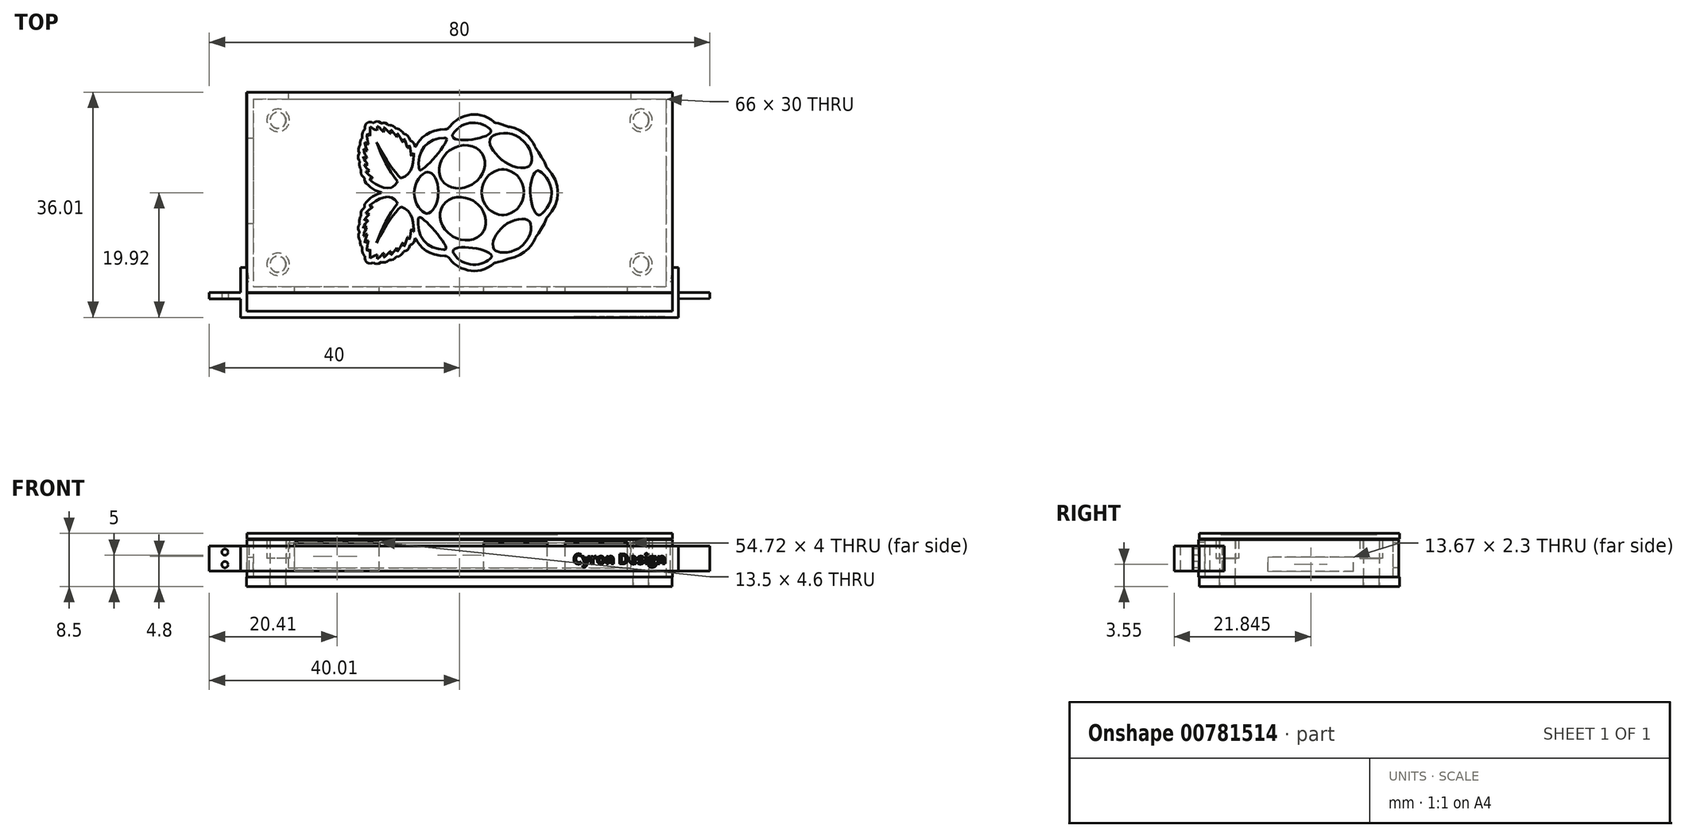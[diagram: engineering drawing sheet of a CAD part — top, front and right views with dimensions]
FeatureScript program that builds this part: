
annotation { "Feature Type Name" : "Feature", "Feature Type Description" : "" }
export const myFeature = defineFeature(function(context is Context, id is Id, definition is map)
    precondition{}
    {
        {
            var Q0;
            Q0=qCreatedBy(makeId("Top.planeOp"),FACE);
            var sketch = newSketch(context, id + "F0", { "sketchPlane" : qUnion([Q0])});
            skLineSegment(sketch, "E0.bottom", {"start": v(-34, 15.91) * mm, "end": v(34, 15.91) * mm});
            skLineSegment(sketch, "E0.top", {"start": v(-34, -16.09) * mm, "end": v(34, -16.09) * mm});
            skLineSegment(sketch, "E0.left", {"start": v(-34, 15.91) * mm, "end": v(-34, -16.09) * mm});
            skLineSegment(sketch, "E0.right", {"start": v(34, 15.91) * mm, "end": v(34, -16.09) * mm});
            skLineSegment(sketch, "E1.bottom", {"start": v(-33, 14.91) * mm, "end": v(33, 14.91) * mm});
            skLineSegment(sketch, "E1.top", {"start": v(-33, -15.09) * mm, "end": v(33, -15.09) * mm});
            skLineSegment(sketch, "E1.left", {"start": v(-33, 14.91) * mm, "end": v(-33, -15.09) * mm});
            skLineSegment(sketch, "E1.right", {"start": v(33, 14.91) * mm, "end": v(33, -15.09) * mm});
            skPoint(sketch, "E2", {"position": v(0, -15.09) * mm});
            skPoint(sketch, "E3", {"position": v(0, -16.09) * mm});
            skPoint(sketch, "E4", {"position": v(0, 14.91) * mm});
            skPoint(sketch, "E5", {"position": v(0, 15.91) * mm});
            skPoint(sketch, "E6", {"position": v(-34, -0.09) * mm});
            skPoint(sketch, "E7", {"position": v(-33, -0.09) * mm});
            skPoint(sketch, "E8", {"position": v(33, -0.09) * mm});
            skPoint(sketch, "E9", {"position": v(34, -0.09) * mm});
            skSolve(sketch);
        }
        {
            var Q0;
            Q0=qCreatedBy(makeId("Top.planeOp"),FACE);
            var sketch = newSketch(context, id + "F1", { "sketchPlane" : qUnion([Q0])});
            skLineSegment(sketch, "E10.bottom", {"start": v(-26.34, -17.54) * mm, "end": v(-12.84, -17.54) * mm});
            skLineSegment(sketch, "E10.top", {"start": v(-26.34, -9.55) * mm, "end": v(-12.84, -9.55) * mm});
            skLineSegment(sketch, "E10.left", {"start": v(-26.34, -17.54) * mm, "end": v(-26.34, -9.55) * mm});
            skLineSegment(sketch, "E10.right", {"start": v(-12.84, -17.54) * mm, "end": v(-12.84, -9.55) * mm});
            skLineSegment(sketch, "E11.bottom", {"start": v(3.84, -17.54) * mm, "end": v(14.02, -17.54) * mm});
            skLineSegment(sketch, "E11.top", {"start": v(3.84, -9.55) * mm, "end": v(14.02, -9.55) * mm});
            skLineSegment(sketch, "E11.left", {"start": v(3.84, -17.54) * mm, "end": v(3.84, -9.55) * mm});
            skLineSegment(sketch, "E11.right", {"start": v(14.02, -17.54) * mm, "end": v(14.02, -9.55) * mm});
            skLineSegment(sketch, "E12.bottom", {"start": v(16.87, -17.41) * mm, "end": v(26.88, -17.41) * mm});
            skLineSegment(sketch, "E12.top", {"start": v(16.87, -9.55) * mm, "end": v(26.88, -9.55) * mm});
            skLineSegment(sketch, "E12.left", {"start": v(16.87, -17.41) * mm, "end": v(16.87, -9.55) * mm});
            skLineSegment(sketch, "E12.right", {"start": v(26.88, -17.41) * mm, "end": v(26.88, -9.55) * mm});
            skSolve(sketch);
        }
        {
            var Q0;
            Q0=qSketchRegion(id+"F0",true);
            extrude(context, id + "F2", {"entities" : qUnion([Q0]), "depth" : 6 * mm, "offsetDistance" : 25 * mm});
        }
        {
            var Q0;
            Q0=qCreatedBy(makeId("Top.planeOp"),FACE);
            var sketch = newSketch(context, id + "F3", { "sketchPlane" : qUnion([Q0])});
            skLineSegment(sketch, "E13.bottom", {"start": v(-35.27, 8.67) * mm, "end": v(-25.56, 8.67) * mm});
            skLineSegment(sketch, "E13.top", {"start": v(-35.27, -5) * mm, "end": v(-25.56, -5) * mm});
            skLineSegment(sketch, "E13.left", {"start": v(-35.27, 8.67) * mm, "end": v(-35.27, -5) * mm});
            skLineSegment(sketch, "E13.right", {"start": v(-25.56, 8.67) * mm, "end": v(-25.56, -5) * mm});
            skSolve(sketch);
        }
        {
            var Q0;
            Q0=qCreatedBy(makeId("Top.planeOp"),FACE);
            var sketch = newSketch(context, id + "F4", { "sketchPlane" : qUnion([Q0])});
            skLineSegment(sketch, "E14.bottom", {"start": v(-27.35, 17.47) * mm, "end": v(27.37, 17.47) * mm});
            skLineSegment(sketch, "E14.top", {"start": v(-27.35, 9.27) * mm, "end": v(27.37, 9.27) * mm});
            skLineSegment(sketch, "E14.left", {"start": v(-27.35, 17.47) * mm, "end": v(-27.35, 9.27) * mm});
            skLineSegment(sketch, "E14.right", {"start": v(27.37, 17.47) * mm, "end": v(27.37, 9.27) * mm});
            skSolve(sketch);
        }
        {
            var Q0;
            Q0=qCreatedBy(makeId("Top.planeOp"),FACE);
            var sketch = newSketch(context, id + "F5", { "sketchPlane" : qUnion([Q0])});
            skLineSegment(sketch, "E15", {"start": v(-34, -12.34) * mm, "end": v(-33.66, -14.34) * mm});
            skLineSegment(sketch, "E16", {"start": v(-33.66, -14.34) * mm, "end": v(-34, -14.34) * mm});
            skLineSegment(sketch, "E17", {"start": v(-34, -14.34) * mm, "end": v(-34, -12.34) * mm});
            skLineSegment(sketch, "E18", {"start": v(-34, -14.34) * mm, "end": v(-33.66, -14.34) * mm});
            skLineSegment(sketch, "E19.MirrorCS", {"start": v(34, -12.34) * mm, "end": v(33.65, -14.34) * mm});
            skLineSegment(sketch, "E20.MirrorCS", {"start": v(34, -14.34) * mm, "end": v(33.65, -14.34) * mm});
            skLineSegment(sketch, "E21.MirrorCS", {"start": v(34, -14.34) * mm, "end": v(34, -12.34) * mm});
            skSolve(sketch);
        }
        {
            var Q0;
            Q0=qSketchRegion(id+"F3",true);
            extrude(context, id + "F6", {"entities" : qUnion([Q0]), "operationType" : NewBodyOperationType.REMOVE, "depth" : 3.2 * mm, "offsetDistance" : 25 * mm, "hasSecondDirection" : true, "secondDirectionOppositeDirection" : false, "secondDirectionDepth" : 0.9 * mm});
        }
        {
            var Q0;
            Q0=qSketchRegion(id+"F1",true);
            extrude(context, id + "F7", {"entities" : qUnion([Q0]), "operationType" : NewBodyOperationType.REMOVE, "depth" : 5.6 * mm, "offsetDistance" : 25 * mm, "hasSecondDirection" : true, "secondDirectionOppositeDirection" : false, "secondDirectionDepth" : 1 * mm});
        }
        {
            var Q0;
            Q0=qSketchRegion(id+"F4",true);
            extrude(context, id + "F8", {"entities" : qUnion([Q0]), "operationType" : NewBodyOperationType.REMOVE, "depth" : 5.5 * mm, "offsetDistance" : 25 * mm, "hasSecondDirection" : true, "secondDirectionOppositeDirection" : false, "secondDirectionDepth" : 1.5 * mm});
        }
        {
            var Q0;
            Q0=qCreatedBy(makeId("Top.planeOp"),FACE);
            var sketch = newSketch(context, id + "F9", { "sketchPlane" : qUnion([Q0])});
            skLineSegment(sketch, "E22.bottom", {"start": v(-34.03, 16) * mm, "end": v(33.97, 16) * mm});
            skLineSegment(sketch, "E22.top", {"start": v(-34.03, -16) * mm, "end": v(33.97, -16) * mm});
            skLineSegment(sketch, "E22.left", {"start": v(-34.03, 16) * mm, "end": v(-34.03, -16) * mm});
            skLineSegment(sketch, "E22.right", {"start": v(33.97, 16) * mm, "end": v(33.97, -16) * mm});
            skCircle(sketch, "E23", {"center": v(-29.03, 11.5) * mm, "radius": 1.25 * mm});
            skCircle(sketch, "E24", {"center": v(28.97, 11.5) * mm, "radius": 1.25 * mm});
            skCircle(sketch, "E25", {"center": v(28.97, -11.5) * mm, "radius": 1.25 * mm});
            skCircle(sketch, "E26", {"center": v(-29.03, -11.5) * mm, "radius": 1.25 * mm});
            skSolve(sketch);
        }
        {
            var Q0;
            Q0=makeQuery(id+"F9.imprint","IMPRINT",FACE,{"disambiguationData":[TD([[makeQuery(id+"F9.imprint","IMPRINT",EDGE,{"derivedFrom":sQuery(id+"F9.wireOp",EDGE,"E26")}),1.0]])]});
            var Q1;
            Q1=makeQuery(id+"F9.imprint","IMPRINT",FACE,{"disambiguationData":[TD([[makeQuery(id+"F9.imprint","IMPRINT",EDGE,{"derivedFrom":sQuery(id+"F9.wireOp",EDGE,"E23")}),1.0]])]});
            var Q2;
            Q2=makeQuery(id+"F9.imprint","IMPRINT",FACE,{"disambiguationData":[TD([[makeQuery(id+"F9.imprint","IMPRINT",EDGE,{"derivedFrom":sQuery(id+"F9.wireOp",EDGE,"E24")}),1.0]])]});
            var Q3;
            Q3=makeQuery(id+"F9.imprint","IMPRINT",FACE,{"disambiguationData":[TD([[makeQuery(id+"F9.imprint","IMPRINT",EDGE,{"derivedFrom":sQuery(id+"F9.wireOp",EDGE,"E25")}),1.0]])]});
            extrude(context, id + "F10", {"entities" : qUnion([Q0, Q1, Q2, Q3]), "depth" : 6 * mm, "offsetDistance" : 25 * mm, "hasSecondDirection" : true, "secondDirectionOppositeDirection" : true, "secondDirectionDepth" : 1.5 * mm});
        }
        {
            var Q0;
            Q0=qSketchRegion(id+"F9",true);
            extrude(context, id + "F11", {"entities" : qUnion([Q0]), "oppositeDirection" : true, "depth" : 1.5 * mm, "offsetDistance" : 25 * mm});
        }
        {
            var Q0;
            Q0=qCreatedBy(makeId("Top.planeOp"),FACE);
            var sketch = newSketch(context, id + "F12", { "sketchPlane" : qUnion([Q0])});
            skLineSegment(sketch, "E27.bottom", {"start": v(-34, 16) * mm, "end": v(34, 16) * mm});
            skLineSegment(sketch, "E27.top", {"start": v(-34, -16) * mm, "end": v(34, -16) * mm});
            skLineSegment(sketch, "E27.left", {"start": v(-34, 16) * mm, "end": v(-34, -16) * mm});
            skLineSegment(sketch, "E27.right", {"start": v(34, 16) * mm, "end": v(34, -16) * mm});
            skCircle(sketch, "E28", {"center": v(-29, 11.5) * mm, "radius": 1.3 * mm});
            skCircle(sketch, "E29", {"center": v(29, 11.5) * mm, "radius": 1.3 * mm});
            skCircle(sketch, "E30", {"center": v(29, -11.5) * mm, "radius": 1.3 * mm});
            skCircle(sketch, "E31", {"center": v(-29, -11.5) * mm, "radius": 1.3 * mm});
            skCircle(sketch, "E32", {"center": v(-29, 11.5) * mm, "radius": 1.8 * mm});
            skCircle(sketch, "E33", {"center": v(-29, -11.5) * mm, "radius": 1.8 * mm});
            skCircle(sketch, "E34", {"center": v(29, 11.5) * mm, "radius": 1.8 * mm});
            skCircle(sketch, "E35", {"center": v(29, -11.5) * mm, "radius": 1.8 * mm});
            skSolve(sketch);
        }
        {
            var Q0;
            Q0=qCreatedBy(makeId("Top.planeOp"),FACE);
            var sketch = newSketch(context, id + "F13", { "sketchPlane" : qUnion([Q0])});
            skLineSegment(sketch, "E36.bottom", {"start": v(-34, -12.01) * mm, "end": v(-35, -12.01) * mm});
            skLineSegment(sketch, "E36.top", {"start": v(-34, -19.01) * mm, "end": v(-35, -19.01) * mm});
            skLineSegment(sketch, "E36.left", {"start": v(-34, -12.01) * mm, "end": v(-34, -19.01) * mm});
            skLineSegment(sketch, "E36.right", {"start": v(-35, -12.01) * mm, "end": v(-35, -19.01) * mm});
            skLineSegment(sketch, "E37.bottom", {"start": v(-35, -17.01) * mm, "end": v(-40, -17.01) * mm});
            skLineSegment(sketch, "E37.top", {"start": v(-35, -16.01) * mm, "end": v(-40, -16.01) * mm});
            skLineSegment(sketch, "E37.left", {"start": v(-35, -17.01) * mm, "end": v(-35, -16.01) * mm});
            skLineSegment(sketch, "E37.right", {"start": v(-40, -17.01) * mm, "end": v(-40, -16.01) * mm});
            skLineSegment(sketch, "E38.MirrorCS", {"start": v(35, -17.01) * mm, "end": v(34.99, -16.01) * mm});
            skLineSegment(sketch, "E39.MirrorCS", {"start": v(34, -12.01) * mm, "end": v(34.97, -12.01) * mm});
            skLineSegment(sketch, "E40.MirrorCS", {"start": v(40, -17) * mm, "end": v(39.99, -16) * mm});
            skLineSegment(sketch, "E41.MirrorCS", {"start": v(34, -19.01) * mm, "end": v(35, -19.01) * mm});
            skLineSegment(sketch, "E42.MirrorCS", {"start": v(35, -17.01) * mm, "end": v(40, -17) * mm});
            skLineSegment(sketch, "E43.MirrorCS", {"start": v(34.99, -16.01) * mm, "end": v(39.99, -16) * mm});
            skLineSegment(sketch, "E44.MirrorCS", {"start": v(34, -12.01) * mm, "end": v(34, -19.01) * mm});
            skLineSegment(sketch, "E45.MirrorCS", {"start": v(34.97, -12.01) * mm, "end": v(35, -19.01) * mm});
            skLineSegment(sketch, "E46.bottom", {"start": v(-35, -19.01) * mm, "end": v(35, -19.01) * mm});
            skLineSegment(sketch, "E46.top", {"start": v(-35, -20.01) * mm, "end": v(35, -20.01) * mm});
            skLineSegment(sketch, "E46.left", {"start": v(-35, -19.01) * mm, "end": v(-35, -20.01) * mm});
            skLineSegment(sketch, "E46.right", {"start": v(35, -19.01) * mm, "end": v(35, -20.01) * mm});
            skLineSegment(sketch, "E47", {"start": v(-34, -12.34) * mm, "end": v(-33.65, -14.34) * mm});
            skLineSegment(sketch, "E48", {"start": v(-33.65, -14.34) * mm, "end": v(-34, -14.34) * mm});
            skLineSegment(sketch, "E49", {"start": v(-34, -14.34) * mm, "end": v(-34, -12.34) * mm});
            skLineSegment(sketch, "E50", {"start": v(-34, -14.34) * mm, "end": v(-33.65, -14.34) * mm});
            skLineSegment(sketch, "E51.MirrorCS", {"start": v(34, -12.34) * mm, "end": v(33.65, -14.34) * mm});
            skLineSegment(sketch, "E52.MirrorCS", {"start": v(34, -14.34) * mm, "end": v(33.65, -14.34) * mm});
            skLineSegment(sketch, "E53.MirrorCS", {"start": v(34, -14.34) * mm, "end": v(34, -12.34) * mm});
            skLineSegment(sketch, "E54.MirrorCS", {"start": v(-34.01, -12.33) * mm, "end": v(-33.66, -14.33) * mm});
            skSolve(sketch);
        }
        {
            var Q0;
            Q0=makeQuery(id+"F13.imprint","IMPRINT",FACE,{"disambiguationData":[TD([[makeQuery(id+"F13.imprint","IMPRINT",EDGE,{"derivedFrom":sQuery(id+"F13.wireOp",EDGE,"E37.bottom")}),-1.0]])]});
            var Q1;
            {var subQ4=sQuery(id+"F13.wireOp",EDGE,"E36.bottom");Q1=makeQuery(id+"F13.imprint","IMPRINT",FACE,{"disambiguationData":[TD([[makeQuery(id+"F13.imprint","IMPRINT",EDGE,{"derivedFrom":subQ4}),1.0]])]});}
            var Q2;
            Q2=makeQuery(id+"F13.imprint","IMPRINT",FACE,{"disambiguationData":[TD([[makeQuery(id+"F13.imprint","IMPRINT",EDGE,{"derivedFrom":sQuery(id+"F13.wireOp",EDGE,"E46.top")}),1.0]])]});
            var Q3;
            Q3=makeQuery(id+"F13.imprint","IMPRINT",FACE,{"disambiguationData":[TD([[makeQuery(id+"F13.imprint","IMPRINT",EDGE,{"derivedFrom":sQuery(id+"F13.wireOp",EDGE,"E40.MirrorCS")}),1.0]])]});
            var Q4;
            {var subQ4=sQuery(id+"F13.wireOp",EDGE,"E39.MirrorCS");Q4=makeQuery(id+"F13.imprint","IMPRINT",FACE,{"disambiguationData":[TD([[makeQuery(id+"F13.imprint","IMPRINT",EDGE,{"derivedFrom":subQ4}),-1.0]])]});}
            var Q5;
            Q5=makeQuery(id+"F13.imprint","IMPRINT",FACE,{"disambiguationData":[TD([[makeQuery(id+"F13.imprint","IMPRINT",EDGE,{"derivedFrom":sQuery(id+"F13.wireOp",EDGE,"E51.MirrorCS")}),1.0]])]});
            var Q6;
            {var subQ0=sQuery(id+"F13.wireOp",EDGE,"E50");var subQ3=sQuery(id+"F13.wireOp",EDGE,"E54.MirrorCS");var subQ5=makeQuery(id+"F13.imprint","INTERSECT",VERTEX,{"derivedFrom":[subQ0,subQ3]});Q6=makeQuery(id+"F13.imprint","IMPRINT",FACE,{"disambiguationData":[TD([[makeQuery(id+"F13.imprint","IMPRINT",EDGE,{"disambiguationData":[TD([[subQ5,1.0]])],"derivedFrom":subQ3}),-1.0]])]});}
            extrude(context, id + "F14", {"entities" : qUnion([Q0, Q1, Q2, Q3, Q4, Q5, Q6]), "depth" : 5 * mm, "offsetDistance" : 25 * mm, "hasSecondDirection" : true, "secondDirectionOppositeDirection" : false, "secondDirectionDepth" : 1 * mm});
        }
        {
            var Q0;
            Q0=makeQuery(id+"F14.opExtrude","SWEPT_FACE",FACE,{"disambiguationData":[OSD([sQuery(id+"F13.wireOp",EDGE,"E37.bottom")])]});
            var sketch = newSketch(context, id + "F15", { "sketchPlane" : qUnion([Q0])});
            skCircle(sketch, "E55", {"center": v(-37.5, 4) * mm, "radius": 0.5 * mm});
            skCircle(sketch, "E56", {"center": v(-37.5, 2) * mm, "radius": 0.5 * mm});
            skSolve(sketch);
        }
        {
            var Q0;
            Q0=sQuery(id+"F15.wireOp",VERTEX,"E55.center");
            var Q1;
            Q1=sQuery(id+"F15.wireOp",VERTEX,"E56.center");
            var Q2;
            Q2=makeQuery(id+"F14.opExtrude","SWEPT_BODY",BODY,{"disambiguationData":[OSD([sQuery(id+"F13.wireOp",EDGE,"E36.bottom"),sQuery(id+"F13.wireOp",EDGE,"E36.left"),sQuery(id+"F13.wireOp",EDGE,"E36.right"),sQuery(id+"F13.wireOp",EDGE,"E37.bottom"),sQuery(id+"F13.wireOp",EDGE,"E37.top"),sQuery(id+"F13.wireOp",EDGE,"E37.right"),sQuery(id+"F13.wireOp",EDGE,"E39.MirrorCS"),sQuery(id+"F13.wireOp",EDGE,"E40.MirrorCS"),sQuery(id+"F13.wireOp",EDGE,"E42.MirrorCS"),sQuery(id+"F13.wireOp",EDGE,"E43.MirrorCS"),sQuery(id+"F13.wireOp",EDGE,"E44.MirrorCS"),sQuery(id+"F13.wireOp",EDGE,"E45.MirrorCS"),sQuery(id+"F13.wireOp",EDGE,"E46.bottom"),sQuery(id+"F13.wireOp",EDGE,"E46.top"),sQuery(id+"F13.wireOp",EDGE,"E46.left"),sQuery(id+"F13.wireOp",EDGE,"E46.right")])]});
            hole(context, id + "F16", {"style" : HoleStyle.SIMPLE, "endStyle" : HoleEndStyle.THROUGH, "holeDiameter" : 1 * mm, "majorDiameter" : 5 * mm, "isTappedThrough" : true, "tappedDepth" : 12 * mm, "tapClearance" : 3, "locations" : qUnion([Q0, Q1]), "scope" : qUnion([Q2])});
        }
        {
            var Q0;
            Q0=makeQuery(id+"F14.opExtrude","SWEPT_FACE",FACE,{"disambiguationData":[OSD([sQuery(id+"F13.wireOp",EDGE,"E42.MirrorCS")])]});
            var sketch = newSketch(context, id + "F17", { "sketchPlane" : qUnion([Q0])});
            skPoint(sketch, "E57", {"position": v(37.48, 4) * mm});
            skPoint(sketch, "E58", {"position": v(37.48, 2) * mm});
            skSolve(sketch);
        }
        {
            var Q0;
            Q0=sQuery(id+"F17.wireOp",VERTEX,"E58");
            var Q1;
            Q1=sQuery(id+"F17.wireOp",VERTEX,"E57");
            var Q2;
            Q2=makeQuery(id+"F14.opExtrude","SWEPT_BODY",BODY,{"disambiguationData":[OSD([sQuery(id+"F13.wireOp",EDGE,"E36.bottom"),sQuery(id+"F13.wireOp",EDGE,"E36.left"),sQuery(id+"F13.wireOp",EDGE,"E36.right"),sQuery(id+"F13.wireOp",EDGE,"E37.bottom"),sQuery(id+"F13.wireOp",EDGE,"E37.top"),sQuery(id+"F13.wireOp",EDGE,"E37.right"),sQuery(id+"F13.wireOp",EDGE,"E39.MirrorCS"),sQuery(id+"F13.wireOp",EDGE,"E40.MirrorCS"),sQuery(id+"F13.wireOp",EDGE,"E42.MirrorCS"),sQuery(id+"F13.wireOp",EDGE,"E43.MirrorCS"),sQuery(id+"F13.wireOp",EDGE,"E44.MirrorCS"),sQuery(id+"F13.wireOp",EDGE,"E45.MirrorCS"),sQuery(id+"F13.wireOp",EDGE,"E46.bottom"),sQuery(id+"F13.wireOp",EDGE,"E46.top"),sQuery(id+"F13.wireOp",EDGE,"E46.left"),sQuery(id+"F13.wireOp",EDGE,"E46.right")])]});
            hole(context, id + "F18", {"style" : HoleStyle.SIMPLE, "endStyle" : HoleEndStyle.THROUGH, "holeDiameter" : 1 * mm, "majorDiameter" : 5 * mm, "isTappedThrough" : true, "tappedDepth" : 12 * mm, "tapClearance" : 3, "locations" : qUnion([Q0, Q1]), "scope" : qUnion([Q2])});
        }
        {
            var Q0;
            Q0=makeQuery(id+"F14.opExtrude","SWEPT_FACE",FACE,{"disambiguationData":[OSD([sQuery(id+"F13.wireOp",EDGE,"E46.top")])]});
            var sketch = newSketch(context, id + "F19", { "sketchPlane" : qUnion([Q0])});
            skText(sketch, "E59", { "text": "Cyron Design", "fontName": "OpenSans-Bold.ttf"});
            const initialGuessF19  = {"E59": [0.01813, 0.0021, 1, 0, 0.00163]};
            skSetInitialGuess(sketch, initialGuessF19);
            skSolve(sketch);
        }
        {
            var Q0;
            Q0 = qSketchRegion(id + "F19", true);
            extrude(context, id + "F20", {"entities" : qUnion([Q0]), "operationType" : NewBodyOperationType.REMOVE, "oppositeDirection" : true, "depth" : .1 * mm, "offsetDistance" : 25 * mm});
        }
        {
            var Q0;
            Q0 = qSketchRegion(id + "F5", true);
            extrude(context, id + "F21", {"entities" : qUnion([Q0]), "operationType" : NewBodyOperationType.REMOVE, "depth" : 5 * mm, "offsetDistance" : 25 * mm, "hasSecondDirection" : true, "secondDirectionOppositeDirection" : false, "secondDirectionDepth" : 1 * mm});
        }
        {
            var Q0;
            Q0=qCreatedBy(makeId("Top.planeOp"),FACE);
            var sketch = newSketch(context, id + "F22", { "sketchPlane" : qUnion([Q0])});
            skLineSegment(sketch, "E60", {"start": v(-16.22, -5.8) * mm, "end": v(-16.22, -5.84) * mm});
            skLineSegment(sketch, "E61", {"start": v(-16.22, -5.84) * mm, "end": v(-16.17, -6.05) * mm});
            skLineSegment(sketch, "E62", {"start": v(-16.17, -6.05) * mm, "end": v(-16.04, -6.28) * mm});
            skLineSegment(sketch, "E63", {"start": v(-16.04, -6.28) * mm, "end": v(-16, -6.33) * mm});
            skLineSegment(sketch, "E64", {"start": v(-16, -6.33) * mm, "end": v(-16.04, -6.42) * mm});
            skLineSegment(sketch, "E65", {"start": v(-16.04, -6.42) * mm, "end": v(-16.12, -6.7) * mm});
            skLineSegment(sketch, "E66", {"start": v(-16.12, -6.7) * mm, "end": v(-16.15, -7.04) * mm});
            skLineSegment(sketch, "E67", {"start": v(-16.15, -7.04) * mm, "end": v(-16.08, -7.38) * mm});
            skLineSegment(sketch, "E68", {"start": v(-16.08, -7.38) * mm, "end": v(-15.94, -7.63) * mm});
            skLineSegment(sketch, "E69", {"start": v(-15.94, -7.63) * mm, "end": v(-15.87, -7.7) * mm});
            skLineSegment(sketch, "E70", {"start": v(-15.87, -7.7) * mm, "end": v(-15.89, -7.8) * mm});
            skLineSegment(sketch, "E71", {"start": v(-15.89, -7.8) * mm, "end": v(-15.9, -8.11) * mm});
            skLineSegment(sketch, "E72", {"start": v(-15.9, -8.11) * mm, "end": v(-15.84, -8.4) * mm});
            skLineSegment(sketch, "E73", {"start": v(-15.84, -8.4) * mm, "end": v(-15.73, -8.58) * mm});
            skLineSegment(sketch, "E74", {"start": v(-15.73, -8.58) * mm, "end": v(-15.62, -8.69) * mm});
            skLineSegment(sketch, "E75", {"start": v(-15.62, -8.69) * mm, "end": v(-15.58, -8.72) * mm});
            skLineSegment(sketch, "E76", {"start": v(-15.58, -8.72) * mm, "end": v(-15.58, -8.74) * mm});
            skLineSegment(sketch, "E77", {"start": v(-15.58, -8.74) * mm, "end": v(-15.59, -8.8) * mm});
            skLineSegment(sketch, "E78", {"start": v(-15.59, -8.8) * mm, "end": v(-15.6, -8.95) * mm});
            skLineSegment(sketch, "E79", {"start": v(-15.6, -8.95) * mm, "end": v(-15.6, -9.14) * mm});
            skLineSegment(sketch, "E80", {"start": v(-15.6, -9.14) * mm, "end": v(-15.58, -9.36) * mm});
            skLineSegment(sketch, "E81", {"start": v(-15.58, -9.36) * mm, "end": v(-15.53, -9.59) * mm});
            skLineSegment(sketch, "E82", {"start": v(-15.53, -9.59) * mm, "end": v(-15.44, -9.81) * mm});
            skLineSegment(sketch, "E83", {"start": v(-15.44, -9.81) * mm, "end": v(-15.3, -10.02) * mm});
            skLineSegment(sketch, "E84", {"start": v(-15.3, -10.02) * mm, "end": v(-15.16, -10.17) * mm});
            skLineSegment(sketch, "E85", {"start": v(-15.16, -10.17) * mm, "end": v(-15.1, -10.2) * mm});
            skLineSegment(sketch, "E86", {"start": v(-15.1, -10.2) * mm, "end": v(-15.11, -10.3) * mm});
            skLineSegment(sketch, "E87", {"start": v(-15.11, -10.3) * mm, "end": v(-15.1, -10.57) * mm});
            skLineSegment(sketch, "E88", {"start": v(-15.1, -10.57) * mm, "end": v(-15.04, -10.86) * mm});
            skLineSegment(sketch, "E89", {"start": v(-15.04, -10.86) * mm, "end": v(-14.92, -11.1) * mm});
            skLineSegment(sketch, "E90", {"start": v(-14.92, -11.1) * mm, "end": v(-14.75, -11.25) * mm});
            skLineSegment(sketch, "E91", {"start": v(-14.75, -11.25) * mm, "end": v(-14.54, -11.35) * mm});
            skLineSegment(sketch, "E92", {"start": v(-14.54, -11.35) * mm, "end": v(-14.3, -11.37) * mm});
            skLineSegment(sketch, "E93", {"start": v(-14.3, -11.37) * mm, "end": v(-14.04, -11.33) * mm});
            skLineSegment(sketch, "E94", {"start": v(-14.04, -11.33) * mm, "end": v(-13.84, -11.25) * mm});
            skLineSegment(sketch, "E95", {"start": v(-13.84, -11.25) * mm, "end": v(-13.78, -11.22) * mm});
            skLineSegment(sketch, "E96", {"start": v(-13.78, -11.22) * mm, "end": v(-13.71, -11.26) * mm});
            skLineSegment(sketch, "E97", {"start": v(-13.71, -11.26) * mm, "end": v(-13.52, -11.37) * mm});
            skLineSegment(sketch, "E98", {"start": v(-13.52, -11.37) * mm, "end": v(-13.24, -11.46) * mm});
            skLineSegment(sketch, "E99", {"start": v(-13.24, -11.46) * mm, "end": v(-12.9, -11.4) * mm});
            skLineSegment(sketch, "E100", {"start": v(-12.9, -11.4) * mm, "end": v(-12.57, -11.23) * mm});
            skLineSegment(sketch, "E101", {"start": v(-12.57, -11.23) * mm, "end": v(-12.47, -11.15) * mm});
            skLineSegment(sketch, "E102", {"start": v(-12.47, -11.15) * mm, "end": v(-12.4, -11.19) * mm});
            skLineSegment(sketch, "E103", {"start": v(-12.4, -11.19) * mm, "end": v(-12.2, -11.23) * mm});
            skLineSegment(sketch, "E104", {"start": v(-12.2, -11.23) * mm, "end": v(-11.9, -11.2) * mm});
            skLineSegment(sketch, "E105", {"start": v(-11.9, -11.2) * mm, "end": v(-11.6, -11.06) * mm});
            skLineSegment(sketch, "E106", {"start": v(-11.6, -11.06) * mm, "end": v(-11.34, -10.87) * mm});
            skLineSegment(sketch, "E107", {"start": v(-11.34, -10.87) * mm, "end": v(-11.26, -10.8) * mm});
            skLineSegment(sketch, "E108", {"start": v(-11.26, -10.8) * mm, "end": v(-11.18, -10.82) * mm});
            skLineSegment(sketch, "E109", {"start": v(-11.18, -10.82) * mm, "end": v(-10.91, -10.82) * mm});
            skLineSegment(sketch, "E110", {"start": v(-10.91, -10.82) * mm, "end": v(-10.61, -10.74) * mm});
            skLineSegment(sketch, "E111", {"start": v(-10.61, -10.74) * mm, "end": v(-10.35, -10.56) * mm});
            skLineSegment(sketch, "E112", {"start": v(-10.35, -10.56) * mm, "end": v(-10.18, -10.37) * mm});
            skLineSegment(sketch, "E113", {"start": v(-10.18, -10.37) * mm, "end": v(-10.13, -10.3) * mm});
            skLineSegment(sketch, "E114", {"start": v(-10.13, -10.3) * mm, "end": v(-10.02, -10.31) * mm});
            skLineSegment(sketch, "E115", {"start": v(-10.02, -10.31) * mm, "end": v(-9.67, -10.23) * mm});
            skLineSegment(sketch, "E116", {"start": v(-9.67, -10.23) * mm, "end": v(-9.32, -9.99) * mm});
            skLineSegment(sketch, "E117", {"start": v(-9.32, -9.99) * mm, "end": v(-9.06, -9.7) * mm});
            skLineSegment(sketch, "E118", {"start": v(-9.06, -9.7) * mm, "end": v(-8.94, -9.51) * mm});
            skLineSegment(sketch, "E119", {"start": v(-8.94, -9.51) * mm, "end": v(-8.9, -9.46) * mm});
            skLineSegment(sketch, "E120", {"start": v(-8.9, -9.46) * mm, "end": v(-8.83, -9.45) * mm});
            skLineSegment(sketch, "E121", {"start": v(-8.83, -9.45) * mm, "end": v(-8.61, -9.38) * mm});
            skLineSegment(sketch, "E122", {"start": v(-8.61, -9.38) * mm, "end": v(-8.34, -9.2) * mm});
            skLineSegment(sketch, "E123", {"start": v(-8.34, -9.2) * mm, "end": v(-8.1, -8.9) * mm});
            skLineSegment(sketch, "E124", {"start": v(-8.1, -8.9) * mm, "end": v(-7.96, -8.54) * mm});
            skLineSegment(sketch, "E125", {"start": v(-7.96, -8.54) * mm, "end": v(-7.92, -8.41) * mm});
            skLineSegment(sketch, "E126", {"start": v(-7.92, -8.41) * mm, "end": v(-7.83, -8.4) * mm});
            skLineSegment(sketch, "E127", {"start": v(-7.83, -8.4) * mm, "end": v(-7.56, -8.25) * mm});
            skLineSegment(sketch, "E128", {"start": v(-7.56, -8.25) * mm, "end": v(-7.33, -8) * mm});
            skLineSegment(sketch, "E129", {"start": v(-7.33, -8) * mm, "end": v(-7.2, -7.68) * mm});
            skLineSegment(sketch, "E130", {"start": v(-7.2, -7.68) * mm, "end": v(-7.12, -7.42) * mm});
            skLineSegment(sketch, "E131", {"start": v(-7.12, -7.42) * mm, "end": v(-7.1, -7.33) * mm});
            skLineSegment(sketch, "E132", {"start": v(-7.1, -7.33) * mm, "end": v(-7.02, -7.48) * mm});
            skLineSegment(sketch, "E133", {"start": v(-7.02, -7.48) * mm, "end": v(-6.75, -7.9) * mm});
            skLineSegment(sketch, "E134", {"start": v(-6.75, -7.9) * mm, "end": v(-6.35, -8.43) * mm});
            skLineSegment(sketch, "E135", {"start": v(-6.35, -8.43) * mm, "end": v(-5.9, -8.92) * mm});
            skLineSegment(sketch, "E136", {"start": v(-5.9, -8.92) * mm, "end": v(-5.36, -9.34) * mm});
            skLineSegment(sketch, "E137", {"start": v(-5.36, -9.34) * mm, "end": v(-4.74, -9.7) * mm});
            skLineSegment(sketch, "E138", {"start": v(-4.74, -9.7) * mm, "end": v(-4, -9.96) * mm});
            skLineSegment(sketch, "E139", {"start": v(-4, -9.96) * mm, "end": v(-3.14, -10.13) * mm});
            skLineSegment(sketch, "E140", {"start": v(-3.14, -10.13) * mm, "end": v(-2.38, -10.19) * mm});
            skLineSegment(sketch, "E141", {"start": v(-2.38, -10.19) * mm, "end": v(-2.13, -10.19) * mm});
            skLineSegment(sketch, "E142", {"start": v(-2.13, -10.19) * mm, "end": v(-1.73, -10.41) * mm});
            skLineSegment(sketch, "E143", {"start": v(-1.73, -10.41) * mm, "end": v(-1.68, -10.5) * mm});
            skLineSegment(sketch, "E144", {"start": v(-1.68, -10.5) * mm, "end": v(-1.5, -10.74) * mm});
            skLineSegment(sketch, "E145", {"start": v(-1.5, -10.74) * mm, "end": v(-1.22, -11.06) * mm});
            skLineSegment(sketch, "E146", {"start": v(-1.22, -11.06) * mm, "end": v(-0.9, -11.36) * mm});
            skLineSegment(sketch, "E147", {"start": v(-0.9, -11.36) * mm, "end": v(-0.52, -11.64) * mm});
            skLineSegment(sketch, "E148", {"start": v(-0.52, -11.64) * mm, "end": v(-0.12, -11.9) * mm});
            skLineSegment(sketch, "E149", {"start": v(-0.12, -11.9) * mm, "end": v(0.33, -12.12) * mm});
            skLineSegment(sketch, "E150", {"start": v(0.33, -12.12) * mm, "end": v(0.8, -12.3) * mm});
            skLineSegment(sketch, "E151", {"start": v(0.8, -12.3) * mm, "end": v(1.3, -12.44) * mm});
            skLineSegment(sketch, "E152", {"start": v(1.3, -12.44) * mm, "end": v(1.8, -12.53) * mm});
            skLineSegment(sketch, "E153", {"start": v(1.8, -12.53) * mm, "end": v(2.34, -12.57) * mm});
            skLineSegment(sketch, "E154", {"start": v(2.34, -12.57) * mm, "end": v(2.88, -12.54) * mm});
            skLineSegment(sketch, "E155", {"start": v(2.88, -12.54) * mm, "end": v(3.43, -12.45) * mm});
            skLineSegment(sketch, "E156", {"start": v(3.43, -12.45) * mm, "end": v(3.98, -12.28) * mm});
            skLineSegment(sketch, "E157", {"start": v(3.98, -12.28) * mm, "end": v(4.53, -12.03) * mm});
            skLineSegment(sketch, "E158", {"start": v(4.53, -12.03) * mm, "end": v(5.08, -11.7) * mm});
            skLineSegment(sketch, "E159", {"start": v(5.08, -11.7) * mm, "end": v(5.48, -11.4) * mm});
            skLineSegment(sketch, "E160", {"start": v(5.48, -11.4) * mm, "end": v(5.61, -11.28) * mm});
            skLineSegment(sketch, "E161", {"start": v(5.61, -11.28) * mm, "end": v(5.77, -11.26) * mm});
            skLineSegment(sketch, "E162", {"start": v(5.77, -11.26) * mm, "end": v(6.23, -11.14) * mm});
            skLineSegment(sketch, "E163", {"start": v(6.23, -11.14) * mm, "end": v(6.78, -10.98) * mm});
            skLineSegment(sketch, "E164", {"start": v(6.78, -10.98) * mm, "end": v(7.3, -10.8) * mm});
            skLineSegment(sketch, "E165", {"start": v(7.3, -10.8) * mm, "end": v(7.69, -10.65) * mm});
            skLineSegment(sketch, "E166", {"start": v(7.69, -10.65) * mm, "end": v(7.82, -10.6) * mm});
            skLineSegment(sketch, "E167", {"start": v(7.82, -10.6) * mm, "end": v(8.07, -10.57) * mm});
            skLineSegment(sketch, "E168", {"start": v(8.07, -10.57) * mm, "end": v(8.8, -10.38) * mm});
            skLineSegment(sketch, "E169", {"start": v(8.8, -10.38) * mm, "end": v(9.66, -10.02) * mm});
            skLineSegment(sketch, "E170", {"start": v(9.66, -10.02) * mm, "end": v(10.37, -9.55) * mm});
            skLineSegment(sketch, "E171", {"start": v(10.37, -9.55) * mm, "end": v(10.96, -9.03) * mm});
            skLineSegment(sketch, "E172", {"start": v(10.96, -9.03) * mm, "end": v(11.43, -8.5) * mm});
            skLineSegment(sketch, "E173", {"start": v(11.43, -8.5) * mm, "end": v(11.77, -7.99) * mm});
            skLineSegment(sketch, "E174", {"start": v(11.77, -7.99) * mm, "end": v(12, -7.56) * mm});
            skLineSegment(sketch, "E175", {"start": v(12, -7.56) * mm, "end": v(12.1, -7.33) * mm});
            skLineSegment(sketch, "E176", {"start": v(12.1, -7.33) * mm, "end": v(12.11, -7.25) * mm});
            skLineSegment(sketch, "E177", {"start": v(12.11, -7.25) * mm, "end": v(12.24, -7.08) * mm});
            skLineSegment(sketch, "E178", {"start": v(12.24, -7.08) * mm, "end": v(12.62, -6.55) * mm});
            skLineSegment(sketch, "E179", {"start": v(12.62, -6.55) * mm, "end": v(13.1, -5.8) * mm});
            skLineSegment(sketch, "E180", {"start": v(13.1, -5.8) * mm, "end": v(13.55, -4.97) * mm});
            skLineSegment(sketch, "E181", {"start": v(13.55, -4.97) * mm, "end": v(13.85, -4.28) * mm});
            skLineSegment(sketch, "E182", {"start": v(13.85, -4.28) * mm, "end": v(13.93, -4.04) * mm});
            skLineSegment(sketch, "E183", {"start": v(13.93, -4.04) * mm, "end": v(14.16, -3.83) * mm});
            skLineSegment(sketch, "E184", {"start": v(14.16, -3.83) * mm, "end": v(14.75, -3.1) * mm});
            skLineSegment(sketch, "E185", {"start": v(14.75, -3.1) * mm, "end": v(15.3, -2.11) * mm});
            skLineSegment(sketch, "E186", {"start": v(15.3, -2.11) * mm, "end": v(15.6, -1.11) * mm});
            skLineSegment(sketch, "E187", {"start": v(15.6, -1.11) * mm, "end": v(15.7, -0.35) * mm});
            skLineSegment(sketch, "E188", {"start": v(15.7, -0.35) * mm, "end": v(15.7, -0.1) * mm});
            skLineSegment(sketch, "E189", {"start": v(15.7, -0.1) * mm, "end": v(15.7, -0.08) * mm});
            skLineSegment(sketch, "E190", {"start": v(15.7, -0.08) * mm, "end": v(15.7, -0.04) * mm});
            skLineSegment(sketch, "E191", {"start": v(15.7, -0.04) * mm, "end": v(15.7, -0.04) * mm});
            skLineSegment(sketch, "E192", {"start": v(15.7, -0.04) * mm, "end": v(15.7, 0.22) * mm});
            skLineSegment(sketch, "E193", {"start": v(15.7, 0.22) * mm, "end": v(15.6, 0.98) * mm});
            skLineSegment(sketch, "E194", {"start": v(15.6, 0.98) * mm, "end": v(15.3, 1.98) * mm});
            skLineSegment(sketch, "E195", {"start": v(15.3, 1.98) * mm, "end": v(14.75, 2.96) * mm});
            skLineSegment(sketch, "E196", {"start": v(14.75, 2.96) * mm, "end": v(14.16, 3.7) * mm});
            skLineSegment(sketch, "E197", {"start": v(14.16, 3.7) * mm, "end": v(13.93, 3.9) * mm});
            skLineSegment(sketch, "E198", {"start": v(13.93, 3.9) * mm, "end": v(13.85, 4.14) * mm});
            skLineSegment(sketch, "E199", {"start": v(13.85, 4.14) * mm, "end": v(13.55, 4.84) * mm});
            skLineSegment(sketch, "E200", {"start": v(13.55, 4.84) * mm, "end": v(13.1, 5.66) * mm});
            skLineSegment(sketch, "E201", {"start": v(13.1, 5.66) * mm, "end": v(12.62, 6.41) * mm});
            skLineSegment(sketch, "E202", {"start": v(12.62, 6.41) * mm, "end": v(12.24, 6.94) * mm});
            skLineSegment(sketch, "E203", {"start": v(12.24, 6.94) * mm, "end": v(12.11, 7.12) * mm});
            skLineSegment(sketch, "E204", {"start": v(12.11, 7.12) * mm, "end": v(12.1, 7.2) * mm});
            skLineSegment(sketch, "E205", {"start": v(12.1, 7.2) * mm, "end": v(12, 7.42) * mm});
            skLineSegment(sketch, "E206", {"start": v(12, 7.42) * mm, "end": v(11.77, 7.85) * mm});
            skLineSegment(sketch, "E207", {"start": v(11.77, 7.85) * mm, "end": v(11.43, 8.36) * mm});
            skLineSegment(sketch, "E208", {"start": v(11.43, 8.36) * mm, "end": v(10.96, 8.9) * mm});
            skLineSegment(sketch, "E209", {"start": v(10.96, 8.9) * mm, "end": v(10.37, 9.42) * mm});
            skLineSegment(sketch, "E210", {"start": v(10.37, 9.42) * mm, "end": v(9.66, 9.88) * mm});
            skLineSegment(sketch, "E211", {"start": v(9.66, 9.88) * mm, "end": v(8.8, 10.25) * mm});
            skLineSegment(sketch, "E212", {"start": v(8.8, 10.25) * mm, "end": v(8.07, 10.44) * mm});
            skLineSegment(sketch, "E213", {"start": v(8.07, 10.44) * mm, "end": v(7.82, 10.47) * mm});
            skLineSegment(sketch, "E214", {"start": v(7.82, 10.47) * mm, "end": v(7.69, 10.52) * mm});
            skLineSegment(sketch, "E215", {"start": v(7.69, 10.52) * mm, "end": v(7.3, 10.66) * mm});
            skLineSegment(sketch, "E216", {"start": v(7.3, 10.66) * mm, "end": v(6.78, 10.84) * mm});
            skLineSegment(sketch, "E217", {"start": v(6.78, 10.84) * mm, "end": v(6.23, 11) * mm});
            skLineSegment(sketch, "E218", {"start": v(6.23, 11) * mm, "end": v(5.77, 11.12) * mm});
            skLineSegment(sketch, "E219", {"start": v(5.77, 11.12) * mm, "end": v(5.61, 11.15) * mm});
            skLineSegment(sketch, "E220", {"start": v(5.61, 11.15) * mm, "end": v(5.48, 11.26) * mm});
            skLineSegment(sketch, "E221", {"start": v(5.48, 11.26) * mm, "end": v(5.08, 11.57) * mm});
            skLineSegment(sketch, "E222", {"start": v(5.08, 11.57) * mm, "end": v(4.53, 11.9) * mm});
            skLineSegment(sketch, "E223", {"start": v(4.53, 11.9) * mm, "end": v(3.98, 12.14) * mm});
            skLineSegment(sketch, "E224", {"start": v(3.98, 12.14) * mm, "end": v(3.43, 12.31) * mm});
            skLineSegment(sketch, "E225", {"start": v(3.43, 12.31) * mm, "end": v(2.88, 12.4) * mm});
            skLineSegment(sketch, "E226", {"start": v(2.88, 12.4) * mm, "end": v(2.34, 12.43) * mm});
            skLineSegment(sketch, "E227", {"start": v(2.34, 12.43) * mm, "end": v(1.8, 12.4) * mm});
            skLineSegment(sketch, "E228", {"start": v(1.8, 12.4) * mm, "end": v(1.3, 12.3) * mm});
            skLineSegment(sketch, "E229", {"start": v(1.3, 12.3) * mm, "end": v(0.8, 12.17) * mm});
            skLineSegment(sketch, "E230", {"start": v(0.8, 12.17) * mm, "end": v(0.32, 11.99) * mm});
            skLineSegment(sketch, "E231", {"start": v(0.32, 11.99) * mm, "end": v(-0.12, 11.76) * mm});
            skLineSegment(sketch, "E232", {"start": v(-0.12, 11.76) * mm, "end": v(-0.52, 11.5) * mm});
            skLineSegment(sketch, "E233", {"start": v(-0.52, 11.5) * mm, "end": v(-0.9, 11.23) * mm});
            skLineSegment(sketch, "E234", {"start": v(-0.9, 11.23) * mm, "end": v(-1.22, 10.92) * mm});
            skLineSegment(sketch, "E235", {"start": v(-1.22, 10.92) * mm, "end": v(-1.5, 10.6) * mm});
            skLineSegment(sketch, "E236", {"start": v(-1.5, 10.6) * mm, "end": v(-1.68, 10.36) * mm});
            skLineSegment(sketch, "E237", {"start": v(-1.68, 10.36) * mm, "end": v(-1.73, 10.28) * mm});
            skLineSegment(sketch, "E238", {"start": v(-1.73, 10.28) * mm, "end": v(-2.13, 10.05) * mm});
            skLineSegment(sketch, "E239", {"start": v(-2.13, 10.05) * mm, "end": v(-2.38, 10.05) * mm});
            skLineSegment(sketch, "E240", {"start": v(-2.38, 10.05) * mm, "end": v(-3.14, 10) * mm});
            skLineSegment(sketch, "E241", {"start": v(-3.14, 10) * mm, "end": v(-4, 9.83) * mm});
            skLineSegment(sketch, "E242", {"start": v(-4, 9.83) * mm, "end": v(-4.74, 9.56) * mm});
            skLineSegment(sketch, "E243", {"start": v(-4.74, 9.56) * mm, "end": v(-5.36, 9.2) * mm});
            skLineSegment(sketch, "E244", {"start": v(-5.36, 9.2) * mm, "end": v(-5.9, 8.78) * mm});
            skLineSegment(sketch, "E245", {"start": v(-5.9, 8.78) * mm, "end": v(-6.35, 8.3) * mm});
            skLineSegment(sketch, "E246", {"start": v(-6.35, 8.3) * mm, "end": v(-6.75, 7.76) * mm});
            skLineSegment(sketch, "E247", {"start": v(-6.75, 7.76) * mm, "end": v(-7.02, 7.34) * mm});
            skLineSegment(sketch, "E248", {"start": v(-7.02, 7.34) * mm, "end": v(-7.1, 7.2) * mm});
            skLineSegment(sketch, "E249", {"start": v(-7.1, 7.2) * mm, "end": v(-7.12, 7.28) * mm});
            skLineSegment(sketch, "E250", {"start": v(-7.12, 7.28) * mm, "end": v(-7.2, 7.54) * mm});
            skLineSegment(sketch, "E251", {"start": v(-7.2, 7.54) * mm, "end": v(-7.34, 7.86) * mm});
            skLineSegment(sketch, "E252", {"start": v(-7.34, 7.86) * mm, "end": v(-7.56, 8.12) * mm});
            skLineSegment(sketch, "E253", {"start": v(-7.56, 8.12) * mm, "end": v(-7.83, 8.26) * mm});
            skLineSegment(sketch, "E254", {"start": v(-7.83, 8.26) * mm, "end": v(-7.92, 8.28) * mm});
            skLineSegment(sketch, "E255", {"start": v(-7.92, 8.28) * mm, "end": v(-7.96, 8.4) * mm});
            skLineSegment(sketch, "E256", {"start": v(-7.96, 8.4) * mm, "end": v(-8.1, 8.77) * mm});
            skLineSegment(sketch, "E257", {"start": v(-8.1, 8.77) * mm, "end": v(-8.34, 9.07) * mm});
            skLineSegment(sketch, "E258", {"start": v(-8.34, 9.07) * mm, "end": v(-8.61, 9.24) * mm});
            skLineSegment(sketch, "E259", {"start": v(-8.61, 9.24) * mm, "end": v(-8.83, 9.31) * mm});
            skLineSegment(sketch, "E260", {"start": v(-8.83, 9.31) * mm, "end": v(-8.9, 9.33) * mm});
            skLineSegment(sketch, "E261", {"start": v(-8.9, 9.33) * mm, "end": v(-8.94, 9.38) * mm});
            skLineSegment(sketch, "E262", {"start": v(-8.94, 9.38) * mm, "end": v(-9.06, 9.56) * mm});
            skLineSegment(sketch, "E263", {"start": v(-9.06, 9.56) * mm, "end": v(-9.32, 9.85) * mm});
            skLineSegment(sketch, "E264", {"start": v(-9.32, 9.85) * mm, "end": v(-9.67, 10.1) * mm});
            skLineSegment(sketch, "E265", {"start": v(-9.67, 10.1) * mm, "end": v(-10.02, 10.18) * mm});
            skLineSegment(sketch, "E266", {"start": v(-10.02, 10.18) * mm, "end": v(-10.13, 10.16) * mm});
            skLineSegment(sketch, "E267", {"start": v(-10.13, 10.16) * mm, "end": v(-10.18, 10.23) * mm});
            skLineSegment(sketch, "E268", {"start": v(-10.18, 10.23) * mm, "end": v(-10.35, 10.42) * mm});
            skLineSegment(sketch, "E269", {"start": v(-10.35, 10.42) * mm, "end": v(-10.61, 10.6) * mm});
            skLineSegment(sketch, "E270", {"start": v(-10.61, 10.6) * mm, "end": v(-10.91, 10.69) * mm});
            skLineSegment(sketch, "E271", {"start": v(-10.91, 10.69) * mm, "end": v(-11.18, 10.68) * mm});
            skLineSegment(sketch, "E272", {"start": v(-11.18, 10.68) * mm, "end": v(-11.26, 10.67) * mm});
            skLineSegment(sketch, "E273", {"start": v(-11.26, 10.67) * mm, "end": v(-11.34, 10.74) * mm});
            skLineSegment(sketch, "E274", {"start": v(-11.34, 10.74) * mm, "end": v(-11.6, 10.92) * mm});
            skLineSegment(sketch, "E275", {"start": v(-11.6, 10.92) * mm, "end": v(-11.9, 11.07) * mm});
            skLineSegment(sketch, "E276", {"start": v(-11.9, 11.07) * mm, "end": v(-12.2, 11.1) * mm});
            skLineSegment(sketch, "E277", {"start": v(-12.2, 11.1) * mm, "end": v(-12.4, 11.05) * mm});
            skLineSegment(sketch, "E278", {"start": v(-12.4, 11.05) * mm, "end": v(-12.47, 11.02) * mm});
            skLineSegment(sketch, "E279", {"start": v(-12.47, 11.02) * mm, "end": v(-12.57, 11.1) * mm});
            skLineSegment(sketch, "E280", {"start": v(-12.57, 11.1) * mm, "end": v(-12.9, 11.27) * mm});
            skLineSegment(sketch, "E281", {"start": v(-12.9, 11.27) * mm, "end": v(-13.24, 11.32) * mm});
            skLineSegment(sketch, "E282", {"start": v(-13.24, 11.32) * mm, "end": v(-13.52, 11.24) * mm});
            skLineSegment(sketch, "E283", {"start": v(-13.52, 11.24) * mm, "end": v(-13.71, 11.12) * mm});
            skLineSegment(sketch, "E284", {"start": v(-13.71, 11.12) * mm, "end": v(-13.78, 11.08) * mm});
            skLineSegment(sketch, "E285", {"start": v(-13.78, 11.08) * mm, "end": v(-13.84, 11.12) * mm});
            skLineSegment(sketch, "E286", {"start": v(-13.84, 11.12) * mm, "end": v(-14.04, 11.2) * mm});
            skLineSegment(sketch, "E287", {"start": v(-14.04, 11.2) * mm, "end": v(-14.3, 11.24) * mm});
            skLineSegment(sketch, "E288", {"start": v(-14.3, 11.24) * mm, "end": v(-14.54, 11.2) * mm});
            skLineSegment(sketch, "E289", {"start": v(-14.54, 11.2) * mm, "end": v(-14.75, 11.12) * mm});
            skLineSegment(sketch, "E290", {"start": v(-14.75, 11.12) * mm, "end": v(-14.92, 10.96) * mm});
            skLineSegment(sketch, "E291", {"start": v(-14.92, 10.96) * mm, "end": v(-15.04, 10.73) * mm});
            skLineSegment(sketch, "E292", {"start": v(-15.04, 10.73) * mm, "end": v(-15.1, 10.43) * mm});
            skLineSegment(sketch, "E293", {"start": v(-15.1, 10.43) * mm, "end": v(-15.11, 10.16) * mm});
            skLineSegment(sketch, "E294", {"start": v(-15.11, 10.16) * mm, "end": v(-15.1, 10.07) * mm});
            skLineSegment(sketch, "E295", {"start": v(-15.1, 10.07) * mm, "end": v(-15.16, 10.03) * mm});
            skLineSegment(sketch, "E296", {"start": v(-15.16, 10.03) * mm, "end": v(-15.3, 9.89) * mm});
            skLineSegment(sketch, "E297", {"start": v(-15.3, 9.89) * mm, "end": v(-15.44, 9.68) * mm});
            skLineSegment(sketch, "E298", {"start": v(-15.44, 9.68) * mm, "end": v(-15.53, 9.45) * mm});
            skLineSegment(sketch, "E299", {"start": v(-15.53, 9.45) * mm, "end": v(-15.58, 9.22) * mm});
            skLineSegment(sketch, "E300", {"start": v(-15.58, 9.22) * mm, "end": v(-15.6, 9) * mm});
            skLineSegment(sketch, "E301", {"start": v(-15.6, 9) * mm, "end": v(-15.6, 8.82) * mm});
            skLineSegment(sketch, "E302", {"start": v(-15.6, 8.82) * mm, "end": v(-15.59, 8.67) * mm});
            skLineSegment(sketch, "E303", {"start": v(-15.59, 8.67) * mm, "end": v(-15.58, 8.6) * mm});
            skLineSegment(sketch, "E304", {"start": v(-15.58, 8.6) * mm, "end": v(-15.58, 8.58) * mm});
            skLineSegment(sketch, "E305", {"start": v(-15.58, 8.58) * mm, "end": v(-15.62, 8.55) * mm});
            skLineSegment(sketch, "E306", {"start": v(-15.62, 8.55) * mm, "end": v(-15.73, 8.45) * mm});
            skLineSegment(sketch, "E307", {"start": v(-15.73, 8.45) * mm, "end": v(-15.84, 8.26) * mm});
            skLineSegment(sketch, "E308", {"start": v(-15.84, 8.26) * mm, "end": v(-15.9, 7.98) * mm});
            skLineSegment(sketch, "E309", {"start": v(-15.9, 7.98) * mm, "end": v(-15.89, 7.67) * mm});
            skLineSegment(sketch, "E310", {"start": v(-15.89, 7.67) * mm, "end": v(-15.87, 7.57) * mm});
            skLineSegment(sketch, "E311", {"start": v(-15.87, 7.57) * mm, "end": v(-15.94, 7.5) * mm});
            skLineSegment(sketch, "E312", {"start": v(-15.94, 7.5) * mm, "end": v(-16.08, 7.24) * mm});
            skLineSegment(sketch, "E313", {"start": v(-16.08, 7.24) * mm, "end": v(-16.15, 6.9) * mm});
            skLineSegment(sketch, "E314", {"start": v(-16.15, 6.9) * mm, "end": v(-16.12, 6.56) * mm});
            skLineSegment(sketch, "E315", {"start": v(-16.12, 6.56) * mm, "end": v(-16.04, 6.28) * mm});
            skLineSegment(sketch, "E316", {"start": v(-16.04, 6.28) * mm, "end": v(-16, 6.2) * mm});
            skLineSegment(sketch, "E317", {"start": v(-16, 6.2) * mm, "end": v(-16.07, 6.11) * mm});
            skLineSegment(sketch, "E318", {"start": v(-16.07, 6.11) * mm, "end": v(-16.2, 5.8) * mm});
            skLineSegment(sketch, "E319", {"start": v(-16.2, 5.8) * mm, "end": v(-16.2, 5.45) * mm});
            skLineSegment(sketch, "E320", {"start": v(-16.2, 5.45) * mm, "end": v(-16.08, 5.13) * mm});
            skLineSegment(sketch, "E321", {"start": v(-16.08, 5.13) * mm, "end": v(-15.98, 4.9) * mm});
            skLineSegment(sketch, "E322", {"start": v(-15.98, 4.9) * mm, "end": v(-15.96, 4.81) * mm});
            skLineSegment(sketch, "E323", {"start": v(-15.96, 4.81) * mm, "end": v(-15.99, 4.7) * mm});
            skLineSegment(sketch, "E324", {"start": v(-15.99, 4.7) * mm, "end": v(-16.04, 4.38) * mm});
            skLineSegment(sketch, "E325", {"start": v(-16.04, 4.38) * mm, "end": v(-15.98, 4.08) * mm});
            skLineSegment(sketch, "E326", {"start": v(-15.98, 4.08) * mm, "end": v(-15.86, 3.85) * mm});
            skLineSegment(sketch, "E327", {"start": v(-15.86, 3.85) * mm, "end": v(-15.77, 3.68) * mm});
            skLineSegment(sketch, "E328", {"start": v(-15.77, 3.68) * mm, "end": v(-15.75, 3.62) * mm});
            skLineSegment(sketch, "E329", {"start": v(-15.75, 3.62) * mm, "end": v(-15.77, 3.5) * mm});
            skLineSegment(sketch, "E330", {"start": v(-15.77, 3.5) * mm, "end": v(-15.78, 3.14) * mm});
            skLineSegment(sketch, "E331", {"start": v(-15.78, 3.14) * mm, "end": v(-15.67, 2.8) * mm});
            skLineSegment(sketch, "E332", {"start": v(-15.67, 2.8) * mm, "end": v(-15.45, 2.52) * mm});
            skLineSegment(sketch, "E333", {"start": v(-15.45, 2.52) * mm, "end": v(-15.25, 2.33) * mm});
            skLineSegment(sketch, "E334", {"start": v(-15.25, 2.33) * mm, "end": v(-15.19, 2.27) * mm});
            skLineSegment(sketch, "E335", {"start": v(-15.19, 2.27) * mm, "end": v(-15.2, 1.84) * mm});
            skLineSegment(sketch, "E336", {"start": v(-15.2, 1.84) * mm, "end": v(-15.14, 1.74) * mm});
            skLineSegment(sketch, "E337", {"start": v(-15.14, 1.74) * mm, "end": v(-14.92, 1.44) * mm});
            skLineSegment(sketch, "E338", {"start": v(-14.92, 1.44) * mm, "end": v(-14.58, 1.1) * mm});
            skLineSegment(sketch, "E339", {"start": v(-14.58, 1.1) * mm, "end": v(-14.22, 0.79) * mm});
            skLineSegment(sketch, "E340", {"start": v(-14.22, 0.79) * mm, "end": v(-13.83, 0.53) * mm});
            skLineSegment(sketch, "E341", {"start": v(-13.83, 0.53) * mm, "end": v(-13.45, 0.32) * mm});
            skLineSegment(sketch, "E342", {"start": v(-13.45, 0.32) * mm, "end": v(-13.08, 0.15) * mm});
            skLineSegment(sketch, "E343", {"start": v(-13.08, 0.15) * mm, "end": v(-12.74, 0.02) * mm});
            skLineSegment(sketch, "E344", {"start": v(-12.74, 0.02) * mm, "end": v(-12.52, -0.05) * mm});
            skLineSegment(sketch, "E345", {"start": v(-12.52, -0.05) * mm, "end": v(-12.45, -0.07) * mm});
            skLineSegment(sketch, "E346", {"start": v(-12.45, -0.07) * mm, "end": v(-12.52, -0.09) * mm});
            skLineSegment(sketch, "E347", {"start": v(-12.52, -0.09) * mm, "end": v(-12.74, -0.16) * mm});
            skLineSegment(sketch, "E348", {"start": v(-12.74, -0.16) * mm, "end": v(-13.08, -0.3) * mm});
            skLineSegment(sketch, "E349", {"start": v(-13.08, -0.3) * mm, "end": v(-13.45, -0.46) * mm});
            skLineSegment(sketch, "E350", {"start": v(-13.45, -0.46) * mm, "end": v(-13.83, -0.67) * mm});
            skLineSegment(sketch, "E351", {"start": v(-13.83, -0.67) * mm, "end": v(-14.22, -0.93) * mm});
            skLineSegment(sketch, "E352", {"start": v(-14.22, -0.93) * mm, "end": v(-14.58, -1.23) * mm});
            skLineSegment(sketch, "E353", {"start": v(-14.58, -1.23) * mm, "end": v(-14.92, -1.58) * mm});
            skLineSegment(sketch, "E354", {"start": v(-14.92, -1.58) * mm, "end": v(-15.14, -1.87) * mm});
            skLineSegment(sketch, "E355", {"start": v(-15.14, -1.87) * mm, "end": v(-15.2, -1.98) * mm});
            skLineSegment(sketch, "E356", {"start": v(-15.2, -1.98) * mm, "end": v(-15.19, -2.4) * mm});
            skLineSegment(sketch, "E357", {"start": v(-15.19, -2.4) * mm, "end": v(-15.25, -2.47) * mm});
            skLineSegment(sketch, "E358", {"start": v(-15.25, -2.47) * mm, "end": v(-15.45, -2.66) * mm});
            skLineSegment(sketch, "E359", {"start": v(-15.45, -2.66) * mm, "end": v(-15.67, -2.93) * mm});
            skLineSegment(sketch, "E360", {"start": v(-15.67, -2.93) * mm, "end": v(-15.78, -3.27) * mm});
            skLineSegment(sketch, "E361", {"start": v(-15.78, -3.27) * mm, "end": v(-15.77, -3.64) * mm});
            skLineSegment(sketch, "E362", {"start": v(-15.77, -3.64) * mm, "end": v(-15.75, -3.75) * mm});
            skLineSegment(sketch, "E363", {"start": v(-15.75, -3.75) * mm, "end": v(-15.77, -3.81) * mm});
            skLineSegment(sketch, "E364", {"start": v(-15.77, -3.81) * mm, "end": v(-15.86, -3.98) * mm});
            skLineSegment(sketch, "E365", {"start": v(-15.86, -3.98) * mm, "end": v(-15.98, -4.22) * mm});
            skLineSegment(sketch, "E366", {"start": v(-15.98, -4.22) * mm, "end": v(-16.04, -4.51) * mm});
            skLineSegment(sketch, "E367", {"start": v(-16.04, -4.51) * mm, "end": v(-15.99, -4.84) * mm});
            skLineSegment(sketch, "E368", {"start": v(-15.99, -4.84) * mm, "end": v(-15.96, -4.95) * mm});
            skLineSegment(sketch, "E369", {"start": v(-15.96, -4.95) * mm, "end": v(-15.97, -5) * mm});
            skLineSegment(sketch, "E370", {"start": v(-15.97, -5) * mm, "end": v(-16.04, -5.16) * mm});
            skLineSegment(sketch, "E371", {"start": v(-16.04, -5.16) * mm, "end": v(-16.13, -5.36) * mm});
            skLineSegment(sketch, "E372", {"start": v(-16.13, -5.36) * mm, "end": v(-16.2, -5.58) * mm});
            skLineSegment(sketch, "E373", {"start": v(-16.2, -5.58) * mm, "end": v(-16.23, -5.74) * mm});
            skLineSegment(sketch, "E374", {"start": v(-16.23, -5.74) * mm, "end": v(-16.22, -5.8) * mm});
            skLineSegment(sketch, "E375", {"start": v(-16.22, -5.8) * mm, "end": v(-16.22, -5.8) * mm});
            skLineSegment(sketch, "E376", {"start": v(-13.26, -8.07) * mm, "end": v(-13.12, -7.8) * mm});
            skLineSegment(sketch, "E377", {"start": v(-13.12, -7.8) * mm, "end": v(-12.69, -7) * mm});
            skLineSegment(sketch, "E378", {"start": v(-12.69, -7) * mm, "end": v(-12.14, -6.03) * mm});
            skLineSegment(sketch, "E379", {"start": v(-12.14, -6.03) * mm, "end": v(-11.62, -5.18) * mm});
            skLineSegment(sketch, "E380", {"start": v(-11.62, -5.18) * mm, "end": v(-11.13, -4.42) * mm});
            skLineSegment(sketch, "E381", {"start": v(-11.13, -4.42) * mm, "end": v(-10.65, -3.76) * mm});
            skLineSegment(sketch, "E382", {"start": v(-10.65, -3.76) * mm, "end": v(-10.2, -3.2) * mm});
            skLineSegment(sketch, "E383", {"start": v(-10.2, -3.2) * mm, "end": v(-9.77, -2.72) * mm});
            skLineSegment(sketch, "E384", {"start": v(-9.77, -2.72) * mm, "end": v(-9.47, -2.41) * mm});
            skLineSegment(sketch, "E385", {"start": v(-9.47, -2.41) * mm, "end": v(-9.36, -2.32) * mm});
            skLineSegment(sketch, "E386", {"start": v(-9.36, -2.32) * mm, "end": v(-9.19, -2.36) * mm});
            skLineSegment(sketch, "E387", {"start": v(-9.19, -2.36) * mm, "end": v(-8.7, -2.6) * mm});
            skLineSegment(sketch, "E388", {"start": v(-8.7, -2.6) * mm, "end": v(-8.2, -3.02) * mm});
            skLineSegment(sketch, "E389", {"start": v(-8.2, -3.02) * mm, "end": v(-7.83, -3.56) * mm});
            skLineSegment(sketch, "E390", {"start": v(-7.83, -3.56) * mm, "end": v(-7.59, -4.16) * mm});
            skLineSegment(sketch, "E391", {"start": v(-7.59, -4.16) * mm, "end": v(-7.43, -4.78) * mm});
            skLineSegment(sketch, "E392", {"start": v(-7.43, -4.78) * mm, "end": v(-7.35, -5.38) * mm});
            skLineSegment(sketch, "E393", {"start": v(-7.35, -5.38) * mm, "end": v(-7.33, -5.9) * mm});
            skLineSegment(sketch, "E394", {"start": v(-7.33, -5.9) * mm, "end": v(-7.34, -6.23) * mm});
            skLineSegment(sketch, "E395", {"start": v(-7.34, -6.23) * mm, "end": v(-7.34, -6.33) * mm});
            skLineSegment(sketch, "E396", {"start": v(-7.34, -6.33) * mm, "end": v(-7.36, -6.3) * mm});
            skLineSegment(sketch, "E397", {"start": v(-7.36, -6.3) * mm, "end": v(-7.41, -6.2) * mm});
            skLineSegment(sketch, "E398", {"start": v(-7.41, -6.2) * mm, "end": v(-7.5, -6.08) * mm});
            skLineSegment(sketch, "E399", {"start": v(-7.5, -6.08) * mm, "end": v(-7.6, -5.98) * mm});
            skLineSegment(sketch, "E400", {"start": v(-7.6, -5.98) * mm, "end": v(-7.67, -5.93) * mm});
            skLineSegment(sketch, "E401", {"start": v(-7.67, -5.93) * mm, "end": v(-7.7, -5.92) * mm});
            skLineSegment(sketch, "E402", {"start": v(-7.7, -5.92) * mm, "end": v(-7.74, -5.98) * mm});
            skLineSegment(sketch, "E403", {"start": v(-7.74, -5.98) * mm, "end": v(-7.78, -6.2) * mm});
            skLineSegment(sketch, "E404", {"start": v(-7.78, -6.2) * mm, "end": v(-7.82, -6.62) * mm});
            skLineSegment(sketch, "E405", {"start": v(-7.82, -6.62) * mm, "end": v(-7.88, -7.1) * mm});
            skLineSegment(sketch, "E406", {"start": v(-7.88, -7.1) * mm, "end": v(-8, -7.47) * mm});
            skLineSegment(sketch, "E407", {"start": v(-8, -7.47) * mm, "end": v(-8.05, -7.58) * mm});
            skLineSegment(sketch, "E408", {"start": v(-8.05, -7.58) * mm, "end": v(-8.06, -7.55) * mm});
            skLineSegment(sketch, "E409", {"start": v(-8.06, -7.55) * mm, "end": v(-8.09, -7.43) * mm});
            skLineSegment(sketch, "E410", {"start": v(-8.09, -7.43) * mm, "end": v(-8.14, -7.32) * mm});
            skLineSegment(sketch, "E411", {"start": v(-8.14, -7.32) * mm, "end": v(-8.2, -7.23) * mm});
            skLineSegment(sketch, "E412", {"start": v(-8.2, -7.23) * mm, "end": v(-8.28, -7.16) * mm});
            skLineSegment(sketch, "E413", {"start": v(-8.28, -7.16) * mm, "end": v(-8.3, -7.15) * mm});
            skLineSegment(sketch, "E414", {"start": v(-8.3, -7.15) * mm, "end": v(-8.34, -7.25) * mm});
            skLineSegment(sketch, "E415", {"start": v(-8.34, -7.25) * mm, "end": v(-8.44, -7.57) * mm});
            skLineSegment(sketch, "E416", {"start": v(-8.44, -7.57) * mm, "end": v(-8.58, -7.97) * mm});
            skLineSegment(sketch, "E417", {"start": v(-8.58, -7.97) * mm, "end": v(-8.74, -8.34) * mm});
            skLineSegment(sketch, "E418", {"start": v(-8.74, -8.34) * mm, "end": v(-8.87, -8.58) * mm});
            skLineSegment(sketch, "E419", {"start": v(-8.87, -8.58) * mm, "end": v(-8.93, -8.65) * mm});
            skLineSegment(sketch, "E420", {"start": v(-8.93, -8.65) * mm, "end": v(-8.93, -8.61) * mm});
            skLineSegment(sketch, "E421", {"start": v(-8.93, -8.61) * mm, "end": v(-8.93, -8.5) * mm});
            skLineSegment(sketch, "E422", {"start": v(-8.93, -8.5) * mm, "end": v(-8.93, -8.36) * mm});
            skLineSegment(sketch, "E423", {"start": v(-8.93, -8.36) * mm, "end": v(-8.97, -8.2) * mm});
            skLineSegment(sketch, "E424", {"start": v(-8.97, -8.2) * mm, "end": v(-9.03, -8.07) * mm});
            skLineSegment(sketch, "E425", {"start": v(-9.03, -8.07) * mm, "end": v(-9.06, -8.03) * mm});
            skLineSegment(sketch, "E426", {"start": v(-9.06, -8.03) * mm, "end": v(-9.13, -8.16) * mm});
            skLineSegment(sketch, "E427", {"start": v(-9.13, -8.16) * mm, "end": v(-9.45, -8.78) * mm});
            skLineSegment(sketch, "E428", {"start": v(-9.45, -8.78) * mm, "end": v(-9.84, -9.37) * mm});
            skLineSegment(sketch, "E429", {"start": v(-9.84, -9.37) * mm, "end": v(-9.95, -9.47) * mm});
            skLineSegment(sketch, "E430", {"start": v(-9.95, -9.47) * mm, "end": v(-9.95, -9.42) * mm});
            skLineSegment(sketch, "E431", {"start": v(-9.95, -9.42) * mm, "end": v(-9.95, -9.28) * mm});
            skLineSegment(sketch, "E432", {"start": v(-9.95, -9.28) * mm, "end": v(-9.96, -9.1) * mm});
            skLineSegment(sketch, "E433", {"start": v(-9.96, -9.1) * mm, "end": v(-9.99, -8.95) * mm});
            skLineSegment(sketch, "E434", {"start": v(-9.99, -8.95) * mm, "end": v(-10.02, -8.87) * mm});
            skLineSegment(sketch, "E435", {"start": v(-10.02, -8.87) * mm, "end": v(-10.04, -8.86) * mm});
            skLineSegment(sketch, "E436", {"start": v(-10.04, -8.86) * mm, "end": v(-10.11, -8.97) * mm});
            skLineSegment(sketch, "E437", {"start": v(-10.11, -8.97) * mm, "end": v(-10.49, -9.48) * mm});
            skLineSegment(sketch, "E438", {"start": v(-10.49, -9.48) * mm, "end": v(-10.9, -9.93) * mm});
            skLineSegment(sketch, "E439", {"start": v(-10.9, -9.93) * mm, "end": v(-10.98, -10.01) * mm});
            skLineSegment(sketch, "E440", {"start": v(-10.98, -10.01) * mm, "end": v(-10.97, -9.95) * mm});
            skLineSegment(sketch, "E441", {"start": v(-10.97, -9.95) * mm, "end": v(-10.96, -9.78) * mm});
            skLineSegment(sketch, "E442", {"start": v(-10.96, -9.78) * mm, "end": v(-10.97, -9.6) * mm});
            skLineSegment(sketch, "E443", {"start": v(-10.97, -9.6) * mm, "end": v(-11, -9.5) * mm});
            skLineSegment(sketch, "E444", {"start": v(-11, -9.5) * mm, "end": v(-11.02, -9.43) * mm});
            skLineSegment(sketch, "E445", {"start": v(-11.02, -9.43) * mm, "end": v(-11.04, -9.41) * mm});
            skLineSegment(sketch, "E446", {"start": v(-11.04, -9.41) * mm, "end": v(-11.1, -9.48) * mm});
            skLineSegment(sketch, "E447", {"start": v(-11.1, -9.48) * mm, "end": v(-11.3, -9.68) * mm});
            skLineSegment(sketch, "E448", {"start": v(-11.3, -9.68) * mm, "end": v(-11.55, -9.96) * mm});
            skLineSegment(sketch, "E449", {"start": v(-11.55, -9.96) * mm, "end": v(-11.81, -10.2) * mm});
            skLineSegment(sketch, "E450", {"start": v(-11.81, -10.2) * mm, "end": v(-12.04, -10.36) * mm});
            skLineSegment(sketch, "E451", {"start": v(-12.04, -10.36) * mm, "end": v(-12.12, -10.4) * mm});
            skLineSegment(sketch, "E452", {"start": v(-12.12, -10.4) * mm, "end": v(-12.1, -10.35) * mm});
            skLineSegment(sketch, "E453", {"start": v(-12.1, -10.35) * mm, "end": v(-12.06, -10.2) * mm});
            skLineSegment(sketch, "E454", {"start": v(-12.06, -10.2) * mm, "end": v(-12.04, -10.02) * mm});
            skLineSegment(sketch, "E455", {"start": v(-12.04, -10.02) * mm, "end": v(-12.05, -9.86) * mm});
            skLineSegment(sketch, "E456", {"start": v(-12.05, -9.86) * mm, "end": v(-12.1, -9.74) * mm});
            skLineSegment(sketch, "E457", {"start": v(-12.1, -9.74) * mm, "end": v(-12.12, -9.71) * mm});
            skLineSegment(sketch, "E458", {"start": v(-12.12, -9.71) * mm, "end": v(-12.18, -9.73) * mm});
            skLineSegment(sketch, "E459", {"start": v(-12.18, -9.73) * mm, "end": v(-12.31, -9.86) * mm});
            skLineSegment(sketch, "E460", {"start": v(-12.31, -9.86) * mm, "end": v(-12.5, -10.1) * mm});
            skLineSegment(sketch, "E461", {"start": v(-12.5, -10.1) * mm, "end": v(-12.77, -10.37) * mm});
            skLineSegment(sketch, "E462", {"start": v(-12.77, -10.37) * mm, "end": v(-13.05, -10.57) * mm});
            skLineSegment(sketch, "E463", {"start": v(-13.05, -10.57) * mm, "end": v(-13.16, -10.61) * mm});
            skLineSegment(sketch, "E464", {"start": v(-13.16, -10.61) * mm, "end": v(-13.15, -10.56) * mm});
            skLineSegment(sketch, "E465", {"start": v(-13.15, -10.56) * mm, "end": v(-13.14, -10.4) * mm});
            skLineSegment(sketch, "E466", {"start": v(-13.14, -10.4) * mm, "end": v(-13.12, -10.21) * mm});
            skLineSegment(sketch, "E467", {"start": v(-13.12, -10.21) * mm, "end": v(-13.13, -10.06) * mm});
            skLineSegment(sketch, "E468", {"start": v(-13.13, -10.06) * mm, "end": v(-13.14, -10) * mm});
            skLineSegment(sketch, "E469", {"start": v(-13.14, -10) * mm, "end": v(-13.16, -9.98) * mm});
            skLineSegment(sketch, "E470", {"start": v(-13.16, -9.98) * mm, "end": v(-13.25, -10) * mm});
            skLineSegment(sketch, "E471", {"start": v(-13.25, -10) * mm, "end": v(-13.51, -10.1) * mm});
            skLineSegment(sketch, "E472", {"start": v(-13.51, -10.1) * mm, "end": v(-13.8, -10.23) * mm});
            skLineSegment(sketch, "E473", {"start": v(-13.8, -10.23) * mm, "end": v(-14.06, -10.39) * mm});
            skLineSegment(sketch, "E474", {"start": v(-14.06, -10.39) * mm, "end": v(-14.24, -10.5) * mm});
            skLineSegment(sketch, "E475", {"start": v(-14.24, -10.5) * mm, "end": v(-14.3, -10.55) * mm});
            skLineSegment(sketch, "E476", {"start": v(-14.3, -10.55) * mm, "end": v(-14.3, -10.43) * mm});
            skLineSegment(sketch, "E477", {"start": v(-14.3, -10.43) * mm, "end": v(-14.3, -10.06) * mm});
            skLineSegment(sketch, "E478", {"start": v(-14.3, -10.06) * mm, "end": v(-14.3, -9.58) * mm});
            skLineSegment(sketch, "E479", {"start": v(-14.3, -9.58) * mm, "end": v(-14.31, -9.2) * mm});
            skLineSegment(sketch, "E480", {"start": v(-14.31, -9.2) * mm, "end": v(-14.34, -9.08) * mm});
            skLineSegment(sketch, "E481", {"start": v(-14.34, -9.08) * mm, "end": v(-14.72, -9.45) * mm});
            skLineSegment(sketch, "E482", {"start": v(-14.72, -9.45) * mm, "end": v(-14.75, -9.35) * mm});
            skLineSegment(sketch, "E483", {"start": v(-14.75, -9.35) * mm, "end": v(-14.78, -9.01) * mm});
            skLineSegment(sketch, "E484", {"start": v(-14.78, -9.01) * mm, "end": v(-14.75, -8.59) * mm});
            skLineSegment(sketch, "E485", {"start": v(-14.75, -8.59) * mm, "end": v(-14.66, -8.19) * mm});
            skLineSegment(sketch, "E486", {"start": v(-14.66, -8.19) * mm, "end": v(-14.59, -7.92) * mm});
            skLineSegment(sketch, "E487", {"start": v(-14.59, -7.92) * mm, "end": v(-14.56, -7.83) * mm});
            skLineSegment(sketch, "E488", {"start": v(-14.56, -7.83) * mm, "end": v(-14.58, -7.8) * mm});
            skLineSegment(sketch, "E489", {"start": v(-14.58, -7.8) * mm, "end": v(-14.68, -7.75) * mm});
            skLineSegment(sketch, "E490", {"start": v(-14.68, -7.75) * mm, "end": v(-14.82, -7.8) * mm});
            skLineSegment(sketch, "E491", {"start": v(-14.82, -7.8) * mm, "end": v(-14.96, -7.9) * mm});
            skLineSegment(sketch, "E492", {"start": v(-14.96, -7.9) * mm, "end": v(-15.07, -8.03) * mm});
            skLineSegment(sketch, "E493", {"start": v(-15.07, -8.03) * mm, "end": v(-15.1, -8.07) * mm});
            skLineSegment(sketch, "E494", {"start": v(-15.1, -8.07) * mm, "end": v(-15.1, -7.95) * mm});
            skLineSegment(sketch, "E495", {"start": v(-15.1, -7.95) * mm, "end": v(-14.97, -7.36) * mm});
            skLineSegment(sketch, "E496", {"start": v(-14.97, -7.36) * mm, "end": v(-14.8, -6.82) * mm});
            skLineSegment(sketch, "E497", {"start": v(-14.8, -6.82) * mm, "end": v(-14.77, -6.72) * mm});
            skLineSegment(sketch, "E498", {"start": v(-14.77, -6.72) * mm, "end": v(-14.8, -6.7) * mm});
            skLineSegment(sketch, "E499", {"start": v(-14.8, -6.7) * mm, "end": v(-14.92, -6.65) * mm});
            skLineSegment(sketch, "E500", {"start": v(-14.92, -6.65) * mm, "end": v(-15.06, -6.73) * mm});
            skLineSegment(sketch, "E501", {"start": v(-15.06, -6.73) * mm, "end": v(-15.21, -6.88) * mm});
            skLineSegment(sketch, "E502", {"start": v(-15.21, -6.88) * mm, "end": v(-15.32, -7) * mm});
            skLineSegment(sketch, "E503", {"start": v(-15.32, -7) * mm, "end": v(-15.36, -7.03) * mm});
            skLineSegment(sketch, "E504", {"start": v(-15.36, -7.03) * mm, "end": v(-15.33, -6.9) * mm});
            skLineSegment(sketch, "E505", {"start": v(-15.33, -6.9) * mm, "end": v(-15.24, -6.53) * mm});
            skLineSegment(sketch, "E506", {"start": v(-15.24, -6.53) * mm, "end": v(-15.1, -6.16) * mm});
            skLineSegment(sketch, "E507", {"start": v(-15.1, -6.16) * mm, "end": v(-14.95, -5.86) * mm});
            skLineSegment(sketch, "E508", {"start": v(-14.95, -5.86) * mm, "end": v(-14.84, -5.68) * mm});
            skLineSegment(sketch, "E509", {"start": v(-14.84, -5.68) * mm, "end": v(-14.8, -5.61) * mm});
            skLineSegment(sketch, "E510", {"start": v(-14.8, -5.61) * mm, "end": v(-14.83, -5.58) * mm});
            skLineSegment(sketch, "E511", {"start": v(-14.83, -5.58) * mm, "end": v(-14.96, -5.52) * mm});
            skLineSegment(sketch, "E512", {"start": v(-14.96, -5.52) * mm, "end": v(-15.12, -5.54) * mm});
            skLineSegment(sketch, "E513", {"start": v(-15.12, -5.54) * mm, "end": v(-15.27, -5.64) * mm});
            skLineSegment(sketch, "E514", {"start": v(-15.27, -5.64) * mm, "end": v(-15.38, -5.73) * mm});
            skLineSegment(sketch, "E515", {"start": v(-15.38, -5.73) * mm, "end": v(-15.41, -5.76) * mm});
            skLineSegment(sketch, "E516", {"start": v(-15.41, -5.76) * mm, "end": v(-15.38, -5.66) * mm});
            skLineSegment(sketch, "E517", {"start": v(-15.38, -5.66) * mm, "end": v(-15.24, -5.37) * mm});
            skLineSegment(sketch, "E518", {"start": v(-15.24, -5.37) * mm, "end": v(-15.05, -5.06) * mm});
            skLineSegment(sketch, "E519", {"start": v(-15.05, -5.06) * mm, "end": v(-14.85, -4.8) * mm});
            skLineSegment(sketch, "E520", {"start": v(-14.85, -4.8) * mm, "end": v(-14.7, -4.63) * mm});
            skLineSegment(sketch, "E521", {"start": v(-14.7, -4.63) * mm, "end": v(-14.65, -4.57) * mm});
            skLineSegment(sketch, "E522", {"start": v(-14.65, -4.57) * mm, "end": v(-14.68, -4.55) * mm});
            skLineSegment(sketch, "E523", {"start": v(-14.68, -4.55) * mm, "end": v(-14.75, -4.48) * mm});
            skLineSegment(sketch, "E524", {"start": v(-14.75, -4.48) * mm, "end": v(-14.87, -4.42) * mm});
            skLineSegment(sketch, "E525", {"start": v(-14.87, -4.42) * mm, "end": v(-15.03, -4.4) * mm});
            skLineSegment(sketch, "E526", {"start": v(-15.03, -4.4) * mm, "end": v(-15.2, -4.46) * mm});
            skLineSegment(sketch, "E527", {"start": v(-15.2, -4.46) * mm, "end": v(-15.24, -4.5) * mm});
            skLineSegment(sketch, "E528", {"start": v(-15.24, -4.5) * mm, "end": v(-15.19, -4.4) * mm});
            skLineSegment(sketch, "E529", {"start": v(-15.19, -4.4) * mm, "end": v(-14.86, -3.95) * mm});
            skLineSegment(sketch, "E530", {"start": v(-14.86, -3.95) * mm, "end": v(-14.5, -3.6) * mm});
            skLineSegment(sketch, "E531", {"start": v(-14.5, -3.6) * mm, "end": v(-14.41, -3.54) * mm});
            skLineSegment(sketch, "E532", {"start": v(-14.41, -3.54) * mm, "end": v(-14.44, -3.5) * mm});
            skLineSegment(sketch, "E533", {"start": v(-14.44, -3.5) * mm, "end": v(-14.55, -3.41) * mm});
            skLineSegment(sketch, "E534", {"start": v(-14.55, -3.41) * mm, "end": v(-14.7, -3.37) * mm});
            skLineSegment(sketch, "E535", {"start": v(-14.7, -3.37) * mm, "end": v(-14.85, -3.38) * mm});
            skLineSegment(sketch, "E536", {"start": v(-14.85, -3.38) * mm, "end": v(-14.96, -3.39) * mm});
            skLineSegment(sketch, "E537", {"start": v(-14.96, -3.39) * mm, "end": v(-15, -3.39) * mm});
            skLineSegment(sketch, "E538", {"start": v(-15, -3.39) * mm, "end": v(-14.92, -3.28) * mm});
            skLineSegment(sketch, "E539", {"start": v(-14.92, -3.28) * mm, "end": v(-14.47, -2.84) * mm});
            skLineSegment(sketch, "E540", {"start": v(-14.47, -2.84) * mm, "end": v(-14.01, -2.44) * mm});
            skLineSegment(sketch, "E541", {"start": v(-14.01, -2.44) * mm, "end": v(-13.92, -2.36) * mm});
            skLineSegment(sketch, "E542", {"start": v(-13.92, -2.36) * mm, "end": v(-13.93, -2.34) * mm});
            skLineSegment(sketch, "E543", {"start": v(-13.93, -2.34) * mm, "end": v(-14.08, -2.26) * mm});
            skLineSegment(sketch, "E544", {"start": v(-14.08, -2.26) * mm, "end": v(-14.33, -2.2) * mm});
            skLineSegment(sketch, "E545", {"start": v(-14.33, -2.2) * mm, "end": v(-14.4, -2.18) * mm});
            skLineSegment(sketch, "E546", {"start": v(-14.4, -2.18) * mm, "end": v(-14.3, -2.07) * mm});
            skLineSegment(sketch, "E547", {"start": v(-14.3, -2.07) * mm, "end": v(-13.96, -1.78) * mm});
            skLineSegment(sketch, "E548", {"start": v(-13.96, -1.78) * mm, "end": v(-13.42, -1.4) * mm});
            skLineSegment(sketch, "E549", {"start": v(-13.42, -1.4) * mm, "end": v(-12.8, -1.06) * mm});
            skLineSegment(sketch, "E550", {"start": v(-12.8, -1.06) * mm, "end": v(-12.16, -0.83) * mm});
            skLineSegment(sketch, "E551", {"start": v(-12.16, -0.83) * mm, "end": v(-11.51, -0.74) * mm});
            skLineSegment(sketch, "E552", {"start": v(-11.51, -0.74) * mm, "end": v(-10.9, -0.84) * mm});
            skLineSegment(sketch, "E553", {"start": v(-10.9, -0.84) * mm, "end": v(-10.36, -1.18) * mm});
            skLineSegment(sketch, "E554", {"start": v(-10.36, -1.18) * mm, "end": v(-10, -1.64) * mm});
            skLineSegment(sketch, "E555", {"start": v(-10, -1.64) * mm, "end": v(-9.92, -1.8) * mm});
            skLineSegment(sketch, "E556", {"start": v(-9.92, -1.8) * mm, "end": v(-10.2, -2.14) * mm});
            skLineSegment(sketch, "E557", {"start": v(-10.2, -2.14) * mm, "end": v(-10.95, -3.2) * mm});
            skLineSegment(sketch, "E558", {"start": v(-10.95, -3.2) * mm, "end": v(-11.84, -4.73) * mm});
            skLineSegment(sketch, "E559", {"start": v(-11.84, -4.73) * mm, "end": v(-12.6, -6.35) * mm});
            skLineSegment(sketch, "E560", {"start": v(-12.6, -6.35) * mm, "end": v(-13.11, -7.64) * mm});
            skLineSegment(sketch, "E561", {"start": v(-13.11, -7.64) * mm, "end": v(-13.26, -8.07) * mm});
            skLineSegment(sketch, "E562", {"start": v(-13.26, 8) * mm, "end": v(-13.12, 7.74) * mm});
            skLineSegment(sketch, "E563", {"start": v(-13.12, 7.74) * mm, "end": v(-12.69, 6.93) * mm});
            skLineSegment(sketch, "E564", {"start": v(-12.69, 6.93) * mm, "end": v(-12.14, 5.97) * mm});
            skLineSegment(sketch, "E565", {"start": v(-12.14, 5.97) * mm, "end": v(-11.62, 5.1) * mm});
            skLineSegment(sketch, "E566", {"start": v(-11.62, 5.1) * mm, "end": v(-11.13, 4.35) * mm});
            skLineSegment(sketch, "E567", {"start": v(-11.13, 4.35) * mm, "end": v(-10.65, 3.7) * mm});
            skLineSegment(sketch, "E568", {"start": v(-10.65, 3.7) * mm, "end": v(-10.2, 3.13) * mm});
            skLineSegment(sketch, "E569", {"start": v(-10.2, 3.13) * mm, "end": v(-9.77, 2.65) * mm});
            skLineSegment(sketch, "E570", {"start": v(-9.77, 2.65) * mm, "end": v(-9.47, 2.35) * mm});
            skLineSegment(sketch, "E571", {"start": v(-9.47, 2.35) * mm, "end": v(-9.36, 2.25) * mm});
            skLineSegment(sketch, "E572", {"start": v(-9.36, 2.25) * mm, "end": v(-9.19, 2.3) * mm});
            skLineSegment(sketch, "E573", {"start": v(-9.19, 2.3) * mm, "end": v(-8.7, 2.53) * mm});
            skLineSegment(sketch, "E574", {"start": v(-8.7, 2.53) * mm, "end": v(-8.2, 2.95) * mm});
            skLineSegment(sketch, "E575", {"start": v(-8.2, 2.95) * mm, "end": v(-7.83, 3.49) * mm});
            skLineSegment(sketch, "E576", {"start": v(-7.83, 3.49) * mm, "end": v(-7.59, 4.09) * mm});
            skLineSegment(sketch, "E577", {"start": v(-7.59, 4.09) * mm, "end": v(-7.43, 4.71) * mm});
            skLineSegment(sketch, "E578", {"start": v(-7.43, 4.71) * mm, "end": v(-7.35, 5.3) * mm});
            skLineSegment(sketch, "E579", {"start": v(-7.35, 5.3) * mm, "end": v(-7.33, 5.84) * mm});
            skLineSegment(sketch, "E580", {"start": v(-7.33, 5.84) * mm, "end": v(-7.34, 6.16) * mm});
            skLineSegment(sketch, "E581", {"start": v(-7.34, 6.16) * mm, "end": v(-7.34, 6.27) * mm});
            skLineSegment(sketch, "E582", {"start": v(-7.34, 6.27) * mm, "end": v(-7.36, 6.23) * mm});
            skLineSegment(sketch, "E583", {"start": v(-7.36, 6.23) * mm, "end": v(-7.41, 6.13) * mm});
            skLineSegment(sketch, "E584", {"start": v(-7.41, 6.13) * mm, "end": v(-7.5, 6) * mm});
            skLineSegment(sketch, "E585", {"start": v(-7.5, 6) * mm, "end": v(-7.6, 5.92) * mm});
            skLineSegment(sketch, "E586", {"start": v(-7.6, 5.92) * mm, "end": v(-7.67, 5.86) * mm});
            skLineSegment(sketch, "E587", {"start": v(-7.67, 5.86) * mm, "end": v(-7.7, 5.85) * mm});
            skLineSegment(sketch, "E588", {"start": v(-7.7, 5.85) * mm, "end": v(-7.74, 5.9) * mm});
            skLineSegment(sketch, "E589", {"start": v(-7.74, 5.9) * mm, "end": v(-7.78, 6.13) * mm});
            skLineSegment(sketch, "E590", {"start": v(-7.78, 6.13) * mm, "end": v(-7.82, 6.55) * mm});
            skLineSegment(sketch, "E591", {"start": v(-7.82, 6.55) * mm, "end": v(-7.88, 7.04) * mm});
            skLineSegment(sketch, "E592", {"start": v(-7.88, 7.04) * mm, "end": v(-8, 7.4) * mm});
            skLineSegment(sketch, "E593", {"start": v(-8, 7.4) * mm, "end": v(-8.05, 7.52) * mm});
            skLineSegment(sketch, "E594", {"start": v(-8.05, 7.52) * mm, "end": v(-8.06, 7.48) * mm});
            skLineSegment(sketch, "E595", {"start": v(-8.06, 7.48) * mm, "end": v(-8.09, 7.37) * mm});
            skLineSegment(sketch, "E596", {"start": v(-8.09, 7.37) * mm, "end": v(-8.14, 7.25) * mm});
            skLineSegment(sketch, "E597", {"start": v(-8.14, 7.25) * mm, "end": v(-8.2, 7.16) * mm});
            skLineSegment(sketch, "E598", {"start": v(-8.2, 7.16) * mm, "end": v(-8.28, 7.1) * mm});
            skLineSegment(sketch, "E599", {"start": v(-8.28, 7.1) * mm, "end": v(-8.3, 7.08) * mm});
            skLineSegment(sketch, "E600", {"start": v(-8.3, 7.08) * mm, "end": v(-8.34, 7.18) * mm});
            skLineSegment(sketch, "E601", {"start": v(-8.34, 7.18) * mm, "end": v(-8.44, 7.5) * mm});
            skLineSegment(sketch, "E602", {"start": v(-8.44, 7.5) * mm, "end": v(-8.58, 7.9) * mm});
            skLineSegment(sketch, "E603", {"start": v(-8.58, 7.9) * mm, "end": v(-8.74, 8.28) * mm});
            skLineSegment(sketch, "E604", {"start": v(-8.74, 8.28) * mm, "end": v(-8.87, 8.51) * mm});
            skLineSegment(sketch, "E605", {"start": v(-8.87, 8.51) * mm, "end": v(-8.93, 8.58) * mm});
            skLineSegment(sketch, "E606", {"start": v(-8.93, 8.58) * mm, "end": v(-8.93, 8.55) * mm});
            skLineSegment(sketch, "E607", {"start": v(-8.93, 8.55) * mm, "end": v(-8.93, 8.44) * mm});
            skLineSegment(sketch, "E608", {"start": v(-8.93, 8.44) * mm, "end": v(-8.93, 8.3) * mm});
            skLineSegment(sketch, "E609", {"start": v(-8.93, 8.3) * mm, "end": v(-8.97, 8.14) * mm});
            skLineSegment(sketch, "E610", {"start": v(-8.97, 8.14) * mm, "end": v(-9.03, 8) * mm});
            skLineSegment(sketch, "E611", {"start": v(-9.03, 8) * mm, "end": v(-9.06, 7.97) * mm});
            skLineSegment(sketch, "E612", {"start": v(-9.06, 7.97) * mm, "end": v(-9.13, 8.1) * mm});
            skLineSegment(sketch, "E613", {"start": v(-9.13, 8.1) * mm, "end": v(-9.45, 8.72) * mm});
            skLineSegment(sketch, "E614", {"start": v(-9.45, 8.72) * mm, "end": v(-9.84, 9.3) * mm});
            skLineSegment(sketch, "E615", {"start": v(-9.84, 9.3) * mm, "end": v(-9.95, 9.4) * mm});
            skLineSegment(sketch, "E616", {"start": v(-9.95, 9.4) * mm, "end": v(-9.95, 9.35) * mm});
            skLineSegment(sketch, "E617", {"start": v(-9.95, 9.35) * mm, "end": v(-9.95, 9.21) * mm});
            skLineSegment(sketch, "E618", {"start": v(-9.95, 9.21) * mm, "end": v(-9.96, 9.03) * mm});
            skLineSegment(sketch, "E619", {"start": v(-9.96, 9.03) * mm, "end": v(-9.99, 8.88) * mm});
            skLineSegment(sketch, "E620", {"start": v(-9.99, 8.88) * mm, "end": v(-10.02, 8.8) * mm});
            skLineSegment(sketch, "E621", {"start": v(-10.02, 8.8) * mm, "end": v(-10.04, 8.8) * mm});
            skLineSegment(sketch, "E622", {"start": v(-10.04, 8.8) * mm, "end": v(-10.11, 8.9) * mm});
            skLineSegment(sketch, "E623", {"start": v(-10.11, 8.9) * mm, "end": v(-10.49, 9.42) * mm});
            skLineSegment(sketch, "E624", {"start": v(-10.49, 9.42) * mm, "end": v(-10.9, 9.86) * mm});
            skLineSegment(sketch, "E625", {"start": v(-10.9, 9.86) * mm, "end": v(-10.98, 9.94) * mm});
            skLineSegment(sketch, "E626", {"start": v(-10.98, 9.94) * mm, "end": v(-10.97, 9.89) * mm});
            skLineSegment(sketch, "E627", {"start": v(-10.97, 9.89) * mm, "end": v(-10.96, 9.71) * mm});
            skLineSegment(sketch, "E628", {"start": v(-10.96, 9.71) * mm, "end": v(-10.97, 9.54) * mm});
            skLineSegment(sketch, "E629", {"start": v(-10.97, 9.54) * mm, "end": v(-11, 9.43) * mm});
            skLineSegment(sketch, "E630", {"start": v(-11, 9.43) * mm, "end": v(-11.02, 9.36) * mm});
            skLineSegment(sketch, "E631", {"start": v(-11.02, 9.36) * mm, "end": v(-11.04, 9.35) * mm});
            skLineSegment(sketch, "E632", {"start": v(-11.04, 9.35) * mm, "end": v(-11.1, 9.41) * mm});
            skLineSegment(sketch, "E633", {"start": v(-11.1, 9.41) * mm, "end": v(-11.3, 9.62) * mm});
            skLineSegment(sketch, "E634", {"start": v(-11.3, 9.62) * mm, "end": v(-11.55, 9.89) * mm});
            skLineSegment(sketch, "E635", {"start": v(-11.55, 9.89) * mm, "end": v(-11.81, 10.14) * mm});
            skLineSegment(sketch, "E636", {"start": v(-11.81, 10.14) * mm, "end": v(-12.04, 10.3) * mm});
            skLineSegment(sketch, "E637", {"start": v(-12.04, 10.3) * mm, "end": v(-12.12, 10.33) * mm});
            skLineSegment(sketch, "E638", {"start": v(-12.12, 10.33) * mm, "end": v(-12.1, 10.28) * mm});
            skLineSegment(sketch, "E639", {"start": v(-12.1, 10.28) * mm, "end": v(-12.06, 10.14) * mm});
            skLineSegment(sketch, "E640", {"start": v(-12.06, 10.14) * mm, "end": v(-12.04, 9.95) * mm});
            skLineSegment(sketch, "E641", {"start": v(-12.04, 9.95) * mm, "end": v(-12.05, 9.79) * mm});
            skLineSegment(sketch, "E642", {"start": v(-12.05, 9.79) * mm, "end": v(-12.1, 9.68) * mm});
            skLineSegment(sketch, "E643", {"start": v(-12.1, 9.68) * mm, "end": v(-12.12, 9.65) * mm});
            skLineSegment(sketch, "E644", {"start": v(-12.12, 9.65) * mm, "end": v(-12.18, 9.67) * mm});
            skLineSegment(sketch, "E645", {"start": v(-12.18, 9.67) * mm, "end": v(-12.31, 9.8) * mm});
            skLineSegment(sketch, "E646", {"start": v(-12.31, 9.8) * mm, "end": v(-12.5, 10.03) * mm});
            skLineSegment(sketch, "E647", {"start": v(-12.5, 10.03) * mm, "end": v(-12.77, 10.3) * mm});
            skLineSegment(sketch, "E648", {"start": v(-12.77, 10.3) * mm, "end": v(-13.05, 10.5) * mm});
            skLineSegment(sketch, "E649", {"start": v(-13.05, 10.5) * mm, "end": v(-13.16, 10.55) * mm});
            skLineSegment(sketch, "E650", {"start": v(-13.16, 10.55) * mm, "end": v(-13.15, 10.5) * mm});
            skLineSegment(sketch, "E651", {"start": v(-13.15, 10.5) * mm, "end": v(-13.14, 10.34) * mm});
            skLineSegment(sketch, "E652", {"start": v(-13.14, 10.34) * mm, "end": v(-13.12, 10.15) * mm});
            skLineSegment(sketch, "E653", {"start": v(-13.12, 10.15) * mm, "end": v(-13.13, 10) * mm});
            skLineSegment(sketch, "E654", {"start": v(-13.13, 10) * mm, "end": v(-13.14, 9.93) * mm});
            skLineSegment(sketch, "E655", {"start": v(-13.14, 9.93) * mm, "end": v(-13.16, 9.91) * mm});
            skLineSegment(sketch, "E656", {"start": v(-13.16, 9.91) * mm, "end": v(-13.25, 9.93) * mm});
            skLineSegment(sketch, "E657", {"start": v(-13.25, 9.93) * mm, "end": v(-13.51, 10.02) * mm});
            skLineSegment(sketch, "E658", {"start": v(-13.51, 10.02) * mm, "end": v(-13.8, 10.16) * mm});
            skLineSegment(sketch, "E659", {"start": v(-13.8, 10.16) * mm, "end": v(-14.06, 10.32) * mm});
            skLineSegment(sketch, "E660", {"start": v(-14.06, 10.32) * mm, "end": v(-14.24, 10.44) * mm});
            skLineSegment(sketch, "E661", {"start": v(-14.24, 10.44) * mm, "end": v(-14.3, 10.48) * mm});
            skLineSegment(sketch, "E662", {"start": v(-14.3, 10.48) * mm, "end": v(-14.3, 10.36) * mm});
            skLineSegment(sketch, "E663", {"start": v(-14.3, 10.36) * mm, "end": v(-14.3, 10) * mm});
            skLineSegment(sketch, "E664", {"start": v(-14.3, 10) * mm, "end": v(-14.3, 9.5) * mm});
            skLineSegment(sketch, "E665", {"start": v(-14.3, 9.5) * mm, "end": v(-14.31, 9.14) * mm});
            skLineSegment(sketch, "E666", {"start": v(-14.31, 9.14) * mm, "end": v(-14.34, 9.02) * mm});
            skLineSegment(sketch, "E667", {"start": v(-14.34, 9.02) * mm, "end": v(-14.72, 9.39) * mm});
            skLineSegment(sketch, "E668", {"start": v(-14.72, 9.39) * mm, "end": v(-14.75, 9.28) * mm});
            skLineSegment(sketch, "E669", {"start": v(-14.75, 9.28) * mm, "end": v(-14.78, 8.95) * mm});
            skLineSegment(sketch, "E670", {"start": v(-14.78, 8.95) * mm, "end": v(-14.75, 8.52) * mm});
            skLineSegment(sketch, "E671", {"start": v(-14.75, 8.52) * mm, "end": v(-14.66, 8.12) * mm});
            skLineSegment(sketch, "E672", {"start": v(-14.66, 8.12) * mm, "end": v(-14.59, 7.85) * mm});
            skLineSegment(sketch, "E673", {"start": v(-14.59, 7.85) * mm, "end": v(-14.56, 7.77) * mm});
            skLineSegment(sketch, "E674", {"start": v(-14.56, 7.77) * mm, "end": v(-14.58, 7.74) * mm});
            skLineSegment(sketch, "E675", {"start": v(-14.58, 7.74) * mm, "end": v(-14.68, 7.69) * mm});
            skLineSegment(sketch, "E676", {"start": v(-14.68, 7.69) * mm, "end": v(-14.82, 7.72) * mm});
            skLineSegment(sketch, "E677", {"start": v(-14.82, 7.72) * mm, "end": v(-14.96, 7.84) * mm});
            skLineSegment(sketch, "E678", {"start": v(-14.96, 7.84) * mm, "end": v(-15.07, 7.97) * mm});
            skLineSegment(sketch, "E679", {"start": v(-15.07, 7.97) * mm, "end": v(-15.1, 8) * mm});
            skLineSegment(sketch, "E680", {"start": v(-15.1, 8) * mm, "end": v(-15.1, 7.88) * mm});
            skLineSegment(sketch, "E681", {"start": v(-15.1, 7.88) * mm, "end": v(-14.97, 7.3) * mm});
            skLineSegment(sketch, "E682", {"start": v(-14.97, 7.3) * mm, "end": v(-14.8, 6.75) * mm});
            skLineSegment(sketch, "E683", {"start": v(-14.8, 6.75) * mm, "end": v(-14.77, 6.65) * mm});
            skLineSegment(sketch, "E684", {"start": v(-14.77, 6.65) * mm, "end": v(-14.8, 6.63) * mm});
            skLineSegment(sketch, "E685", {"start": v(-14.8, 6.63) * mm, "end": v(-14.92, 6.59) * mm});
            skLineSegment(sketch, "E686", {"start": v(-14.92, 6.59) * mm, "end": v(-15.06, 6.66) * mm});
            skLineSegment(sketch, "E687", {"start": v(-15.06, 6.66) * mm, "end": v(-15.21, 6.81) * mm});
            skLineSegment(sketch, "E688", {"start": v(-15.21, 6.81) * mm, "end": v(-15.32, 6.93) * mm});
            skLineSegment(sketch, "E689", {"start": v(-15.32, 6.93) * mm, "end": v(-15.36, 6.97) * mm});
            skLineSegment(sketch, "E690", {"start": v(-15.36, 6.97) * mm, "end": v(-15.33, 6.84) * mm});
            skLineSegment(sketch, "E691", {"start": v(-15.33, 6.84) * mm, "end": v(-15.24, 6.47) * mm});
            skLineSegment(sketch, "E692", {"start": v(-15.24, 6.47) * mm, "end": v(-15.1, 6.1) * mm});
            skLineSegment(sketch, "E693", {"start": v(-15.1, 6.1) * mm, "end": v(-14.95, 5.8) * mm});
            skLineSegment(sketch, "E694", {"start": v(-14.95, 5.8) * mm, "end": v(-14.84, 5.61) * mm});
            skLineSegment(sketch, "E695", {"start": v(-14.84, 5.61) * mm, "end": v(-14.8, 5.55) * mm});
            skLineSegment(sketch, "E696", {"start": v(-14.8, 5.55) * mm, "end": v(-14.83, 5.51) * mm});
            skLineSegment(sketch, "E697", {"start": v(-14.83, 5.51) * mm, "end": v(-14.97, 5.45) * mm});
            skLineSegment(sketch, "E698", {"start": v(-14.97, 5.45) * mm, "end": v(-15.12, 5.47) * mm});
            skLineSegment(sketch, "E699", {"start": v(-15.12, 5.47) * mm, "end": v(-15.27, 5.57) * mm});
            skLineSegment(sketch, "E700", {"start": v(-15.27, 5.57) * mm, "end": v(-15.38, 5.66) * mm});
            skLineSegment(sketch, "E701", {"start": v(-15.38, 5.66) * mm, "end": v(-15.41, 5.7) * mm});
            skLineSegment(sketch, "E702", {"start": v(-15.41, 5.7) * mm, "end": v(-15.38, 5.6) * mm});
            skLineSegment(sketch, "E703", {"start": v(-15.38, 5.6) * mm, "end": v(-15.24, 5.3) * mm});
            skLineSegment(sketch, "E704", {"start": v(-15.24, 5.3) * mm, "end": v(-15.05, 5) * mm});
            skLineSegment(sketch, "E705", {"start": v(-15.05, 5) * mm, "end": v(-14.85, 4.74) * mm});
            skLineSegment(sketch, "E706", {"start": v(-14.85, 4.74) * mm, "end": v(-14.7, 4.56) * mm});
            skLineSegment(sketch, "E707", {"start": v(-14.7, 4.56) * mm, "end": v(-14.65, 4.5) * mm});
            skLineSegment(sketch, "E708", {"start": v(-14.65, 4.5) * mm, "end": v(-14.68, 4.48) * mm});
            skLineSegment(sketch, "E709", {"start": v(-14.68, 4.48) * mm, "end": v(-14.75, 4.42) * mm});
            skLineSegment(sketch, "E710", {"start": v(-14.75, 4.42) * mm, "end": v(-14.87, 4.35) * mm});
            skLineSegment(sketch, "E711", {"start": v(-14.87, 4.35) * mm, "end": v(-15.03, 4.34) * mm});
            skLineSegment(sketch, "E712", {"start": v(-15.03, 4.34) * mm, "end": v(-15.2, 4.4) * mm});
            skLineSegment(sketch, "E713", {"start": v(-15.2, 4.4) * mm, "end": v(-15.25, 4.43) * mm});
            skLineSegment(sketch, "E714", {"start": v(-15.25, 4.43) * mm, "end": v(-15.19, 4.32) * mm});
            skLineSegment(sketch, "E715", {"start": v(-15.19, 4.32) * mm, "end": v(-14.86, 3.88) * mm});
            skLineSegment(sketch, "E716", {"start": v(-14.86, 3.88) * mm, "end": v(-14.5, 3.53) * mm});
            skLineSegment(sketch, "E717", {"start": v(-14.5, 3.53) * mm, "end": v(-14.41, 3.48) * mm});
            skLineSegment(sketch, "E718", {"start": v(-14.41, 3.48) * mm, "end": v(-14.44, 3.44) * mm});
            skLineSegment(sketch, "E719", {"start": v(-14.44, 3.44) * mm, "end": v(-14.55, 3.34) * mm});
            skLineSegment(sketch, "E720", {"start": v(-14.55, 3.34) * mm, "end": v(-14.7, 3.3) * mm});
            skLineSegment(sketch, "E721", {"start": v(-14.7, 3.3) * mm, "end": v(-14.85, 3.31) * mm});
            skLineSegment(sketch, "E722", {"start": v(-14.85, 3.31) * mm, "end": v(-14.96, 3.32) * mm});
            skLineSegment(sketch, "E723", {"start": v(-14.96, 3.32) * mm, "end": v(-15, 3.32) * mm});
            skLineSegment(sketch, "E724", {"start": v(-15, 3.32) * mm, "end": v(-14.92, 3.22) * mm});
            skLineSegment(sketch, "E725", {"start": v(-14.92, 3.22) * mm, "end": v(-14.47, 2.77) * mm});
            skLineSegment(sketch, "E726", {"start": v(-14.47, 2.77) * mm, "end": v(-14.01, 2.37) * mm});
            skLineSegment(sketch, "E727", {"start": v(-14.01, 2.37) * mm, "end": v(-13.92, 2.3) * mm});
            skLineSegment(sketch, "E728", {"start": v(-13.92, 2.3) * mm, "end": v(-13.94, 2.27) * mm});
            skLineSegment(sketch, "E729", {"start": v(-13.94, 2.27) * mm, "end": v(-14.08, 2.2) * mm});
            skLineSegment(sketch, "E730", {"start": v(-14.08, 2.2) * mm, "end": v(-14.33, 2.13) * mm});
            skLineSegment(sketch, "E731", {"start": v(-14.33, 2.13) * mm, "end": v(-14.4, 2.11) * mm});
            skLineSegment(sketch, "E732", {"start": v(-14.4, 2.11) * mm, "end": v(-14.3, 2) * mm});
            skLineSegment(sketch, "E733", {"start": v(-14.3, 2) * mm, "end": v(-13.96, 1.72) * mm});
            skLineSegment(sketch, "E734", {"start": v(-13.96, 1.72) * mm, "end": v(-13.42, 1.33) * mm});
            skLineSegment(sketch, "E735", {"start": v(-13.42, 1.33) * mm, "end": v(-12.8, 1) * mm});
            skLineSegment(sketch, "E736", {"start": v(-12.8, 1) * mm, "end": v(-12.16, 0.76) * mm});
            skLineSegment(sketch, "E737", {"start": v(-12.16, 0.76) * mm, "end": v(-11.51, 0.67) * mm});
            skLineSegment(sketch, "E738", {"start": v(-11.51, 0.67) * mm, "end": v(-10.9, 0.77) * mm});
            skLineSegment(sketch, "E739", {"start": v(-10.9, 0.77) * mm, "end": v(-10.36, 1.11) * mm});
            skLineSegment(sketch, "E740", {"start": v(-10.36, 1.11) * mm, "end": v(-10, 1.57) * mm});
            skLineSegment(sketch, "E741", {"start": v(-10, 1.57) * mm, "end": v(-9.92, 1.74) * mm});
            skLineSegment(sketch, "E742", {"start": v(-9.92, 1.74) * mm, "end": v(-10.2, 2.08) * mm});
            skLineSegment(sketch, "E743", {"start": v(-10.2, 2.08) * mm, "end": v(-10.95, 3.14) * mm});
            skLineSegment(sketch, "E744", {"start": v(-10.95, 3.14) * mm, "end": v(-11.84, 4.66) * mm});
            skLineSegment(sketch, "E745", {"start": v(-11.84, 4.66) * mm, "end": v(-12.6, 6.28) * mm});
            skLineSegment(sketch, "E746", {"start": v(-12.6, 6.28) * mm, "end": v(-13.11, 7.57) * mm});
            skLineSegment(sketch, "E747", {"start": v(-13.11, 7.57) * mm, "end": v(-13.26, 8) * mm});
            skLineSegment(sketch, "E748", {"start": v(6.91, 3.64) * mm, "end": v(7.08, 3.64) * mm});
            skLineSegment(sketch, "E749", {"start": v(7.08, 3.64) * mm, "end": v(7.57, 3.57) * mm});
            skLineSegment(sketch, "E750", {"start": v(7.57, 3.57) * mm, "end": v(8.2, 3.37) * mm});
            skLineSegment(sketch, "E751", {"start": v(8.2, 3.37) * mm, "end": v(8.78, 3.03) * mm});
            skLineSegment(sketch, "E752", {"start": v(8.78, 3.03) * mm, "end": v(9.18, 2.7) * mm});
            skLineSegment(sketch, "E753", {"start": v(9.18, 2.7) * mm, "end": v(9.3, 2.58) * mm});
            skLineSegment(sketch, "E754", {"start": v(9.3, 2.58) * mm, "end": v(9.41, 2.45) * mm});
            skLineSegment(sketch, "E755", {"start": v(9.41, 2.45) * mm, "end": v(9.71, 2.03) * mm});
            skLineSegment(sketch, "E756", {"start": v(9.71, 2.03) * mm, "end": v(10.02, 1.4) * mm});
            skLineSegment(sketch, "E757", {"start": v(10.02, 1.4) * mm, "end": v(10.21, 0.72) * mm});
            skLineSegment(sketch, "E758", {"start": v(10.21, 0.72) * mm, "end": v(10.28, 0.18) * mm});
            skLineSegment(sketch, "E759", {"start": v(10.28, 0.18) * mm, "end": v(10.28, 0) * mm});
            skLineSegment(sketch, "E760", {"start": v(10.28, 0) * mm, "end": v(10.28, -0.17) * mm});
            skLineSegment(sketch, "E761", {"start": v(10.28, -0.17) * mm, "end": v(10.21, -0.7) * mm});
            skLineSegment(sketch, "E762", {"start": v(10.21, -0.7) * mm, "end": v(10.02, -1.39) * mm});
            skLineSegment(sketch, "E763", {"start": v(10.02, -1.39) * mm, "end": v(9.71, -2.01) * mm});
            skLineSegment(sketch, "E764", {"start": v(9.71, -2.01) * mm, "end": v(9.41, -2.44) * mm});
            skLineSegment(sketch, "E765", {"start": v(9.41, -2.44) * mm, "end": v(9.3, -2.57) * mm});
            skLineSegment(sketch, "E766", {"start": v(9.3, -2.57) * mm, "end": v(9.18, -2.7) * mm});
            skLineSegment(sketch, "E767", {"start": v(9.18, -2.7) * mm, "end": v(8.78, -3.02) * mm});
            skLineSegment(sketch, "E768", {"start": v(8.78, -3.02) * mm, "end": v(8.2, -3.35) * mm});
            skLineSegment(sketch, "E769", {"start": v(8.2, -3.35) * mm, "end": v(7.57, -3.56) * mm});
            skLineSegment(sketch, "E770", {"start": v(7.57, -3.56) * mm, "end": v(7.08, -3.63) * mm});
            skLineSegment(sketch, "E771", {"start": v(7.08, -3.63) * mm, "end": v(6.91, -3.62) * mm});
            skLineSegment(sketch, "E772", {"start": v(6.91, -3.62) * mm, "end": v(6.75, -3.63) * mm});
            skLineSegment(sketch, "E773", {"start": v(6.75, -3.63) * mm, "end": v(6.26, -3.56) * mm});
            skLineSegment(sketch, "E774", {"start": v(6.26, -3.56) * mm, "end": v(5.63, -3.35) * mm});
            skLineSegment(sketch, "E775", {"start": v(5.63, -3.35) * mm, "end": v(5.05, -3.02) * mm});
            skLineSegment(sketch, "E776", {"start": v(5.05, -3.02) * mm, "end": v(4.65, -2.7) * mm});
            skLineSegment(sketch, "E777", {"start": v(4.65, -2.7) * mm, "end": v(4.54, -2.57) * mm});
            skLineSegment(sketch, "E778", {"start": v(4.54, -2.57) * mm, "end": v(4.42, -2.44) * mm});
            skLineSegment(sketch, "E779", {"start": v(4.42, -2.44) * mm, "end": v(4.12, -2.01) * mm});
            skLineSegment(sketch, "E780", {"start": v(4.12, -2.01) * mm, "end": v(3.8, -1.39) * mm});
            skLineSegment(sketch, "E781", {"start": v(3.8, -1.39) * mm, "end": v(3.61, -0.7) * mm});
            skLineSegment(sketch, "E782", {"start": v(3.61, -0.7) * mm, "end": v(3.55, -0.17) * mm});
            skLineSegment(sketch, "E783", {"start": v(3.55, -0.17) * mm, "end": v(3.55, 0) * mm});
            skLineSegment(sketch, "E784", {"start": v(3.55, 0) * mm, "end": v(3.55, 0.18) * mm});
            skLineSegment(sketch, "E785", {"start": v(3.55, 0.18) * mm, "end": v(3.61, 0.72) * mm});
            skLineSegment(sketch, "E786", {"start": v(3.61, 0.72) * mm, "end": v(3.8, 1.4) * mm});
            skLineSegment(sketch, "E787", {"start": v(3.8, 1.4) * mm, "end": v(4.12, 2.03) * mm});
            skLineSegment(sketch, "E788", {"start": v(4.12, 2.03) * mm, "end": v(4.42, 2.45) * mm});
            skLineSegment(sketch, "E789", {"start": v(4.42, 2.45) * mm, "end": v(4.54, 2.58) * mm});
            skLineSegment(sketch, "E790", {"start": v(4.54, 2.58) * mm, "end": v(4.65, 2.7) * mm});
            skLineSegment(sketch, "E791", {"start": v(4.65, 2.7) * mm, "end": v(5.05, 3.03) * mm});
            skLineSegment(sketch, "E792", {"start": v(5.05, 3.03) * mm, "end": v(5.63, 3.37) * mm});
            skLineSegment(sketch, "E793", {"start": v(5.63, 3.37) * mm, "end": v(6.26, 3.57) * mm});
            skLineSegment(sketch, "E794", {"start": v(6.26, 3.57) * mm, "end": v(6.75, 3.64) * mm});
            skLineSegment(sketch, "E795", {"start": v(6.75, 3.64) * mm, "end": v(6.91, 3.64) * mm});
            skLineSegment(sketch, "E796", {"start": v(-2.65, -2.1) * mm, "end": v(-2.56, -1.96) * mm});
            skLineSegment(sketch, "E797", {"start": v(-2.56, -1.96) * mm, "end": v(-2.22, -1.59) * mm});
            skLineSegment(sketch, "E798", {"start": v(-2.22, -1.59) * mm, "end": v(-1.7, -1.2) * mm});
            skLineSegment(sketch, "E799", {"start": v(-1.7, -1.2) * mm, "end": v(-1.1, -0.93) * mm});
            skLineSegment(sketch, "E800", {"start": v(-1.1, -0.93) * mm, "end": v(-0.45, -0.79) * mm});
            skLineSegment(sketch, "E801", {"start": v(-0.45, -0.79) * mm, "end": v(0.24, -0.77) * mm});
            skLineSegment(sketch, "E802", {"start": v(0.24, -0.77) * mm, "end": v(0.95, -0.88) * mm});
            skLineSegment(sketch, "E803", {"start": v(0.95, -0.88) * mm, "end": v(1.66, -1.12) * mm});
            skLineSegment(sketch, "E804", {"start": v(1.66, -1.12) * mm, "end": v(2.18, -1.38) * mm});
            skLineSegment(sketch, "E805", {"start": v(2.18, -1.38) * mm, "end": v(2.34, -1.49) * mm});
            skLineSegment(sketch, "E806", {"start": v(2.34, -1.49) * mm, "end": v(2.5, -1.6) * mm});
            skLineSegment(sketch, "E807", {"start": v(2.5, -1.6) * mm, "end": v(2.95, -1.97) * mm});
            skLineSegment(sketch, "E808", {"start": v(2.95, -1.97) * mm, "end": v(3.45, -2.53) * mm});
            skLineSegment(sketch, "E809", {"start": v(3.45, -2.53) * mm, "end": v(3.83, -3.14) * mm});
            skLineSegment(sketch, "E810", {"start": v(3.83, -3.14) * mm, "end": v(4.08, -3.78) * mm});
            skLineSegment(sketch, "E811", {"start": v(4.08, -3.78) * mm, "end": v(4.21, -4.45) * mm});
            skLineSegment(sketch, "E812", {"start": v(4.21, -4.45) * mm, "end": v(4.2, -5.1) * mm});
            skLineSegment(sketch, "E813", {"start": v(4.2, -5.1) * mm, "end": v(4.06, -5.74) * mm});
            skLineSegment(sketch, "E814", {"start": v(4.06, -5.74) * mm, "end": v(3.85, -6.2) * mm});
            skLineSegment(sketch, "E815", {"start": v(3.85, -6.2) * mm, "end": v(3.76, -6.33) * mm});
            skLineSegment(sketch, "E816", {"start": v(3.76, -6.33) * mm, "end": v(3.67, -6.47) * mm});
            skLineSegment(sketch, "E817", {"start": v(3.67, -6.47) * mm, "end": v(3.34, -6.84) * mm});
            skLineSegment(sketch, "E818", {"start": v(3.34, -6.84) * mm, "end": v(2.82, -7.22) * mm});
            skLineSegment(sketch, "E819", {"start": v(2.82, -7.22) * mm, "end": v(2.22, -7.5) * mm});
            skLineSegment(sketch, "E820", {"start": v(2.22, -7.5) * mm, "end": v(1.56, -7.64) * mm});
            skLineSegment(sketch, "E821", {"start": v(1.56, -7.64) * mm, "end": v(0.87, -7.66) * mm});
            skLineSegment(sketch, "E822", {"start": v(0.87, -7.66) * mm, "end": v(0.16, -7.55) * mm});
            skLineSegment(sketch, "E823", {"start": v(0.16, -7.55) * mm, "end": v(-0.55, -7.3) * mm});
            skLineSegment(sketch, "E824", {"start": v(-0.55, -7.3) * mm, "end": v(-1.07, -7.04) * mm});
            skLineSegment(sketch, "E825", {"start": v(-1.07, -7.04) * mm, "end": v(-1.23, -6.94) * mm});
            skLineSegment(sketch, "E826", {"start": v(-1.23, -6.94) * mm, "end": v(-1.39, -6.83) * mm});
            skLineSegment(sketch, "E827", {"start": v(-1.39, -6.83) * mm, "end": v(-1.84, -6.45) * mm});
            skLineSegment(sketch, "E828", {"start": v(-1.84, -6.45) * mm, "end": v(-2.34, -5.9) * mm});
            skLineSegment(sketch, "E829", {"start": v(-2.34, -5.9) * mm, "end": v(-2.72, -5.29) * mm});
            skLineSegment(sketch, "E830", {"start": v(-2.72, -5.29) * mm, "end": v(-2.97, -4.64) * mm});
            skLineSegment(sketch, "E831", {"start": v(-2.97, -4.64) * mm, "end": v(-3.1, -3.98) * mm});
            skLineSegment(sketch, "E832", {"start": v(-3.1, -3.98) * mm, "end": v(-3.1, -3.32) * mm});
            skLineSegment(sketch, "E833", {"start": v(-3.1, -3.32) * mm, "end": v(-2.94, -2.69) * mm});
            skLineSegment(sketch, "E834", {"start": v(-2.94, -2.69) * mm, "end": v(-2.74, -2.23) * mm});
            skLineSegment(sketch, "E835", {"start": v(-2.74, -2.23) * mm, "end": v(-2.65, -2.1) * mm});
            skLineSegment(sketch, "E836", {"start": v(-2.83, 1.97) * mm, "end": v(-2.74, 1.83) * mm});
            skLineSegment(sketch, "E837", {"start": v(-2.74, 1.83) * mm, "end": v(-2.4, 1.46) * mm});
            skLineSegment(sketch, "E838", {"start": v(-2.4, 1.46) * mm, "end": v(-1.88, 1.07) * mm});
            skLineSegment(sketch, "E839", {"start": v(-1.88, 1.07) * mm, "end": v(-1.28, 0.8) * mm});
            skLineSegment(sketch, "E840", {"start": v(-1.28, 0.8) * mm, "end": v(-0.63, 0.66) * mm});
            skLineSegment(sketch, "E841", {"start": v(-0.63, 0.66) * mm, "end": v(0.07, 0.64) * mm});
            skLineSegment(sketch, "E842", {"start": v(0.07, 0.64) * mm, "end": v(0.77, 0.75) * mm});
            skLineSegment(sketch, "E843", {"start": v(0.77, 0.75) * mm, "end": v(1.48, 0.99) * mm});
            skLineSegment(sketch, "E844", {"start": v(1.48, 0.99) * mm, "end": v(2, 1.25) * mm});
            skLineSegment(sketch, "E845", {"start": v(2, 1.25) * mm, "end": v(2.16, 1.36) * mm});
            skLineSegment(sketch, "E846", {"start": v(2.16, 1.36) * mm, "end": v(2.32, 1.47) * mm});
            skLineSegment(sketch, "E847", {"start": v(2.32, 1.47) * mm, "end": v(2.77, 1.84) * mm});
            skLineSegment(sketch, "E848", {"start": v(2.77, 1.84) * mm, "end": v(3.27, 2.4) * mm});
            skLineSegment(sketch, "E849", {"start": v(3.27, 2.4) * mm, "end": v(3.65, 3) * mm});
            skLineSegment(sketch, "E850", {"start": v(3.65, 3) * mm, "end": v(3.9, 3.66) * mm});
            skLineSegment(sketch, "E851", {"start": v(3.9, 3.66) * mm, "end": v(4.03, 4.32) * mm});
            skLineSegment(sketch, "E852", {"start": v(4.03, 4.32) * mm, "end": v(4.03, 4.98) * mm});
            skLineSegment(sketch, "E853", {"start": v(4.03, 4.98) * mm, "end": v(3.88, 5.61) * mm});
            skLineSegment(sketch, "E854", {"start": v(3.88, 5.61) * mm, "end": v(3.67, 6.06) * mm});
            skLineSegment(sketch, "E855", {"start": v(3.67, 6.06) * mm, "end": v(3.58, 6.2) * mm});
            skLineSegment(sketch, "E856", {"start": v(3.58, 6.2) * mm, "end": v(3.5, 6.34) * mm});
            skLineSegment(sketch, "E857", {"start": v(3.5, 6.34) * mm, "end": v(3.16, 6.7) * mm});
            skLineSegment(sketch, "E858", {"start": v(3.16, 6.7) * mm, "end": v(2.64, 7.1) * mm});
            skLineSegment(sketch, "E859", {"start": v(2.64, 7.1) * mm, "end": v(2.04, 7.36) * mm});
            skLineSegment(sketch, "E860", {"start": v(2.04, 7.36) * mm, "end": v(1.38, 7.5) * mm});
            skLineSegment(sketch, "E861", {"start": v(1.38, 7.5) * mm, "end": v(0.7, 7.53) * mm});
            skLineSegment(sketch, "E862", {"start": v(0.7, 7.53) * mm, "end": v(-0.02, 7.42) * mm});
            skLineSegment(sketch, "E863", {"start": v(-0.02, 7.42) * mm, "end": v(-0.72, 7.18) * mm});
            skLineSegment(sketch, "E864", {"start": v(-0.72, 7.18) * mm, "end": v(-1.25, 6.91) * mm});
            skLineSegment(sketch, "E865", {"start": v(-1.25, 6.91) * mm, "end": v(-1.4, 6.8) * mm});
            skLineSegment(sketch, "E866", {"start": v(-1.4, 6.8) * mm, "end": v(-1.57, 6.7) * mm});
            skLineSegment(sketch, "E867", {"start": v(-1.57, 6.7) * mm, "end": v(-2.02, 6.33) * mm});
            skLineSegment(sketch, "E868", {"start": v(-2.02, 6.33) * mm, "end": v(-2.51, 5.77) * mm});
            skLineSegment(sketch, "E869", {"start": v(-2.51, 5.77) * mm, "end": v(-2.9, 5.16) * mm});
            skLineSegment(sketch, "E870", {"start": v(-2.9, 5.16) * mm, "end": v(-3.15, 4.51) * mm});
            skLineSegment(sketch, "E871", {"start": v(-3.15, 4.51) * mm, "end": v(-3.28, 3.85) * mm});
            skLineSegment(sketch, "E872", {"start": v(-3.28, 3.85) * mm, "end": v(-3.27, 3.2) * mm});
            skLineSegment(sketch, "E873", {"start": v(-3.27, 3.2) * mm, "end": v(-3.12, 2.56) * mm});
            skLineSegment(sketch, "E874", {"start": v(-3.12, 2.56) * mm, "end": v(-2.92, 2.1) * mm});
            skLineSegment(sketch, "E875", {"start": v(-2.92, 2.1) * mm, "end": v(-2.83, 1.97) * mm});
            skLineSegment(sketch, "E876", {"start": v(-1.04, -9.61) * mm, "end": v(-1.05, -9.55) * mm});
            skLineSegment(sketch, "E877", {"start": v(-1.05, -9.55) * mm, "end": v(-1.03, -9.34) * mm});
            skLineSegment(sketch, "E878", {"start": v(-1.03, -9.34) * mm, "end": v(-0.88, -9.13) * mm});
            skLineSegment(sketch, "E879", {"start": v(-0.88, -9.13) * mm, "end": v(-0.58, -8.97) * mm});
            skLineSegment(sketch, "E880", {"start": v(-0.58, -8.97) * mm, "end": v(-0.18, -8.86) * mm});
            skLineSegment(sketch, "E881", {"start": v(-0.18, -8.86) * mm, "end": v(0.3, -8.8) * mm});
            skLineSegment(sketch, "E882", {"start": v(0.3, -8.8) * mm, "end": v(0.87, -8.8) * mm});
            skLineSegment(sketch, "E883", {"start": v(0.87, -8.8) * mm, "end": v(1.47, -8.83) * mm});
            skLineSegment(sketch, "E884", {"start": v(1.47, -8.83) * mm, "end": v(2.09, -8.9) * mm});
            skLineSegment(sketch, "E885", {"start": v(2.09, -8.9) * mm, "end": v(2.7, -9) * mm});
            skLineSegment(sketch, "E886", {"start": v(2.7, -9) * mm, "end": v(3.3, -9.13) * mm});
            skLineSegment(sketch, "E887", {"start": v(3.3, -9.13) * mm, "end": v(3.84, -9.3) * mm});
            skLineSegment(sketch, "E888", {"start": v(3.84, -9.3) * mm, "end": v(4.32, -9.48) * mm});
            skLineSegment(sketch, "E889", {"start": v(4.32, -9.48) * mm, "end": v(4.7, -9.68) * mm});
            skLineSegment(sketch, "E890", {"start": v(4.7, -9.68) * mm, "end": v(4.98, -9.9) * mm});
            skLineSegment(sketch, "E891", {"start": v(4.98, -9.9) * mm, "end": v(5.12, -10.14) * mm});
            skLineSegment(sketch, "E892", {"start": v(5.12, -10.14) * mm, "end": v(5.12, -10.33) * mm});
            skLineSegment(sketch, "E893", {"start": v(5.12, -10.33) * mm, "end": v(5.1, -10.39) * mm});
            skLineSegment(sketch, "E894", {"start": v(5.1, -10.39) * mm, "end": v(5.04, -10.46) * mm});
            skLineSegment(sketch, "E895", {"start": v(5.04, -10.46) * mm, "end": v(4.85, -10.65) * mm});
            skLineSegment(sketch, "E896", {"start": v(4.85, -10.65) * mm, "end": v(4.56, -10.88) * mm});
            skLineSegment(sketch, "E897", {"start": v(4.56, -10.88) * mm, "end": v(4.23, -11.09) * mm});
            skLineSegment(sketch, "E898", {"start": v(4.23, -11.09) * mm, "end": v(3.86, -11.26) * mm});
            skLineSegment(sketch, "E899", {"start": v(3.86, -11.26) * mm, "end": v(3.46, -11.4) * mm});
            skLineSegment(sketch, "E900", {"start": v(3.46, -11.4) * mm, "end": v(3.05, -11.5) * mm});
            skLineSegment(sketch, "E901", {"start": v(3.05, -11.5) * mm, "end": v(2.61, -11.55) * mm});
            skLineSegment(sketch, "E902", {"start": v(2.61, -11.55) * mm, "end": v(2.17, -11.55) * mm});
            skLineSegment(sketch, "E903", {"start": v(2.17, -11.55) * mm, "end": v(1.72, -11.52) * mm});
            skLineSegment(sketch, "E904", {"start": v(1.72, -11.52) * mm, "end": v(1.27, -11.42) * mm});
            skLineSegment(sketch, "E905", {"start": v(1.27, -11.42) * mm, "end": v(0.83, -11.28) * mm});
            skLineSegment(sketch, "E906", {"start": v(0.83, -11.28) * mm, "end": v(0.4, -11.07) * mm});
            skLineSegment(sketch, "E907", {"start": v(0.4, -11.07) * mm, "end": v(0, -10.8) * mm});
            skLineSegment(sketch, "E908", {"start": v(0, -10.8) * mm, "end": v(-0.38, -10.48) * mm});
            skLineSegment(sketch, "E909", {"start": v(-0.38, -10.48) * mm, "end": v(-0.73, -10.08) * mm});
            skLineSegment(sketch, "E910", {"start": v(-0.73, -10.08) * mm, "end": v(-0.97, -9.73) * mm});
            skLineSegment(sketch, "E911", {"start": v(-0.97, -9.73) * mm, "end": v(-1.04, -9.61) * mm});
            skLineSegment(sketch, "E912", {"start": v(-1.13, 9.16) * mm, "end": v(-1.14, 9.1) * mm});
            skLineSegment(sketch, "E913", {"start": v(-1.14, 9.1) * mm, "end": v(-1.12, 8.88) * mm});
            skLineSegment(sketch, "E914", {"start": v(-1.12, 8.88) * mm, "end": v(-0.96, 8.67) * mm});
            skLineSegment(sketch, "E915", {"start": v(-0.96, 8.67) * mm, "end": v(-0.67, 8.51) * mm});
            skLineSegment(sketch, "E916", {"start": v(-0.67, 8.51) * mm, "end": v(-0.27, 8.4) * mm});
            skLineSegment(sketch, "E917", {"start": v(-0.27, 8.4) * mm, "end": v(0.22, 8.35) * mm});
            skLineSegment(sketch, "E918", {"start": v(0.22, 8.35) * mm, "end": v(0.78, 8.34) * mm});
            skLineSegment(sketch, "E919", {"start": v(0.78, 8.34) * mm, "end": v(1.38, 8.37) * mm});
            skLineSegment(sketch, "E920", {"start": v(1.38, 8.37) * mm, "end": v(2, 8.44) * mm});
            skLineSegment(sketch, "E921", {"start": v(2, 8.44) * mm, "end": v(2.61, 8.54) * mm});
            skLineSegment(sketch, "E922", {"start": v(2.61, 8.54) * mm, "end": v(3.2, 8.68) * mm});
            skLineSegment(sketch, "E923", {"start": v(3.2, 8.68) * mm, "end": v(3.76, 8.84) * mm});
            skLineSegment(sketch, "E924", {"start": v(3.76, 8.84) * mm, "end": v(4.23, 9.02) * mm});
            skLineSegment(sketch, "E925", {"start": v(4.23, 9.02) * mm, "end": v(4.62, 9.23) * mm});
            skLineSegment(sketch, "E926", {"start": v(4.62, 9.23) * mm, "end": v(4.9, 9.45) * mm});
            skLineSegment(sketch, "E927", {"start": v(4.9, 9.45) * mm, "end": v(5.03, 9.69) * mm});
            skLineSegment(sketch, "E928", {"start": v(5.03, 9.69) * mm, "end": v(5.03, 9.88) * mm});
            skLineSegment(sketch, "E929", {"start": v(5.03, 9.88) * mm, "end": v(5, 9.93) * mm});
            skLineSegment(sketch, "E930", {"start": v(5, 9.93) * mm, "end": v(4.95, 10) * mm});
            skLineSegment(sketch, "E931", {"start": v(4.95, 10) * mm, "end": v(4.76, 10.2) * mm});
            skLineSegment(sketch, "E932", {"start": v(4.76, 10.2) * mm, "end": v(4.47, 10.42) * mm});
            skLineSegment(sketch, "E933", {"start": v(4.47, 10.42) * mm, "end": v(4.14, 10.63) * mm});
            skLineSegment(sketch, "E934", {"start": v(4.14, 10.63) * mm, "end": v(3.77, 10.8) * mm});
            skLineSegment(sketch, "E935", {"start": v(3.77, 10.8) * mm, "end": v(3.38, 10.94) * mm});
            skLineSegment(sketch, "E936", {"start": v(3.38, 10.94) * mm, "end": v(2.96, 11.03) * mm});
            skLineSegment(sketch, "E937", {"start": v(2.96, 11.03) * mm, "end": v(2.52, 11.09) * mm});
            skLineSegment(sketch, "E938", {"start": v(2.52, 11.09) * mm, "end": v(2.08, 11.1) * mm});
            skLineSegment(sketch, "E939", {"start": v(2.08, 11.1) * mm, "end": v(1.63, 11.06) * mm});
            skLineSegment(sketch, "E940", {"start": v(1.63, 11.06) * mm, "end": v(1.18, 10.97) * mm});
            skLineSegment(sketch, "E941", {"start": v(1.18, 10.97) * mm, "end": v(0.74, 10.82) * mm});
            skLineSegment(sketch, "E942", {"start": v(0.74, 10.82) * mm, "end": v(0.32, 10.62) * mm});
            skLineSegment(sketch, "E943", {"start": v(0.32, 10.62) * mm, "end": v(-0.09, 10.35) * mm});
            skLineSegment(sketch, "E944", {"start": v(-0.09, 10.35) * mm, "end": v(-0.47, 10.02) * mm});
            skLineSegment(sketch, "E945", {"start": v(-0.47, 10.02) * mm, "end": v(-0.82, 9.63) * mm});
            skLineSegment(sketch, "E946", {"start": v(-0.82, 9.63) * mm, "end": v(-1.06, 9.28) * mm});
            skLineSegment(sketch, "E947", {"start": v(-1.06, 9.28) * mm, "end": v(-1.13, 9.16) * mm});
            skLineSegment(sketch, "E948", {"start": v(-6.45, 3.64) * mm, "end": v(-6.5, 3.9) * mm});
            skLineSegment(sketch, "E949", {"start": v(-6.5, 3.9) * mm, "end": v(-6.53, 4.66) * mm});
            skLineSegment(sketch, "E950", {"start": v(-6.53, 4.66) * mm, "end": v(-6.42, 5.62) * mm});
            skLineSegment(sketch, "E951", {"start": v(-6.42, 5.62) * mm, "end": v(-6.13, 6.49) * mm});
            skLineSegment(sketch, "E952", {"start": v(-6.13, 6.49) * mm, "end": v(-5.66, 7.25) * mm});
            skLineSegment(sketch, "E953", {"start": v(-5.66, 7.25) * mm, "end": v(-5.02, 7.86) * mm});
            skLineSegment(sketch, "E954", {"start": v(-5.02, 7.86) * mm, "end": v(-4.23, 8.33) * mm});
            skLineSegment(sketch, "E955", {"start": v(-4.23, 8.33) * mm, "end": v(-3.3, 8.6) * mm});
            skLineSegment(sketch, "E956", {"start": v(-3.3, 8.6) * mm, "end": v(-2.5, 8.69) * mm});
            skLineSegment(sketch, "E957", {"start": v(-2.5, 8.69) * mm, "end": v(-2.22, 8.68) * mm});
            skLineSegment(sketch, "E958", {"start": v(-2.22, 8.68) * mm, "end": v(-2.19, 8.68) * mm});
            skLineSegment(sketch, "E959", {"start": v(-2.19, 8.68) * mm, "end": v(-2.08, 8.6) * mm});
            skLineSegment(sketch, "E960", {"start": v(-2.08, 8.6) * mm, "end": v(-2.06, 8.4) * mm});
            skLineSegment(sketch, "E961", {"start": v(-2.06, 8.4) * mm, "end": v(-2.17, 8.1) * mm});
            skLineSegment(sketch, "E962", {"start": v(-2.17, 8.1) * mm, "end": v(-2.37, 7.7) * mm});
            skLineSegment(sketch, "E963", {"start": v(-2.37, 7.7) * mm, "end": v(-2.65, 7.26) * mm});
            skLineSegment(sketch, "E964", {"start": v(-2.65, 7.26) * mm, "end": v(-3, 6.77) * mm});
            skLineSegment(sketch, "E965", {"start": v(-3, 6.77) * mm, "end": v(-3.4, 6.26) * mm});
            skLineSegment(sketch, "E966", {"start": v(-3.4, 6.26) * mm, "end": v(-3.84, 5.74) * mm});
            skLineSegment(sketch, "E967", {"start": v(-3.84, 5.74) * mm, "end": v(-4.29, 5.23) * mm});
            skLineSegment(sketch, "E968", {"start": v(-4.29, 5.23) * mm, "end": v(-4.73, 4.76) * mm});
            skLineSegment(sketch, "E969", {"start": v(-4.73, 4.76) * mm, "end": v(-5.16, 4.33) * mm});
            skLineSegment(sketch, "E970", {"start": v(-5.16, 4.33) * mm, "end": v(-5.56, 3.98) * mm});
            skLineSegment(sketch, "E971", {"start": v(-5.56, 3.98) * mm, "end": v(-5.9, 3.71) * mm});
            skLineSegment(sketch, "E972", {"start": v(-5.9, 3.71) * mm, "end": v(-6.18, 3.55) * mm});
            skLineSegment(sketch, "E973", {"start": v(-6.18, 3.55) * mm, "end": v(-6.37, 3.52) * mm});
            skLineSegment(sketch, "E974", {"start": v(-6.37, 3.52) * mm, "end": v(-6.45, 3.6) * mm});
            skLineSegment(sketch, "E975", {"start": v(-6.45, 3.6) * mm, "end": v(-6.45, 3.64) * mm});
            skLineSegment(sketch, "E976", {"start": v(-6.54, -4.1) * mm, "end": v(-6.59, -4.36) * mm});
            skLineSegment(sketch, "E977", {"start": v(-6.59, -4.36) * mm, "end": v(-6.62, -5.13) * mm});
            skLineSegment(sketch, "E978", {"start": v(-6.62, -5.13) * mm, "end": v(-6.5, -6.09) * mm});
            skLineSegment(sketch, "E979", {"start": v(-6.5, -6.09) * mm, "end": v(-6.21, -6.96) * mm});
            skLineSegment(sketch, "E980", {"start": v(-6.21, -6.96) * mm, "end": v(-5.75, -7.71) * mm});
            skLineSegment(sketch, "E981", {"start": v(-5.75, -7.71) * mm, "end": v(-5.11, -8.33) * mm});
            skLineSegment(sketch, "E982", {"start": v(-5.11, -8.33) * mm, "end": v(-4.32, -8.8) * mm});
            skLineSegment(sketch, "E983", {"start": v(-4.32, -8.8) * mm, "end": v(-3.39, -9.07) * mm});
            skLineSegment(sketch, "E984", {"start": v(-3.39, -9.07) * mm, "end": v(-2.58, -9.16) * mm});
            skLineSegment(sketch, "E985", {"start": v(-2.58, -9.16) * mm, "end": v(-2.31, -9.15) * mm});
            skLineSegment(sketch, "E986", {"start": v(-2.31, -9.15) * mm, "end": v(-2.27, -9.14) * mm});
            skLineSegment(sketch, "E987", {"start": v(-2.27, -9.14) * mm, "end": v(-2.17, -9.06) * mm});
            skLineSegment(sketch, "E988", {"start": v(-2.17, -9.06) * mm, "end": v(-2.15, -8.86) * mm});
            skLineSegment(sketch, "E989", {"start": v(-2.15, -8.86) * mm, "end": v(-2.26, -8.56) * mm});
            skLineSegment(sketch, "E990", {"start": v(-2.26, -8.56) * mm, "end": v(-2.46, -8.18) * mm});
            skLineSegment(sketch, "E991", {"start": v(-2.46, -8.18) * mm, "end": v(-2.74, -7.73) * mm});
            skLineSegment(sketch, "E992", {"start": v(-2.74, -7.73) * mm, "end": v(-3.1, -7.24) * mm});
            skLineSegment(sketch, "E993", {"start": v(-3.1, -7.24) * mm, "end": v(-3.5, -6.72) * mm});
            skLineSegment(sketch, "E994", {"start": v(-3.5, -6.72) * mm, "end": v(-3.93, -6.2) * mm});
            skLineSegment(sketch, "E995", {"start": v(-3.93, -6.2) * mm, "end": v(-4.37, -5.7) * mm});
            skLineSegment(sketch, "E996", {"start": v(-4.37, -5.7) * mm, "end": v(-4.82, -5.22) * mm});
            skLineSegment(sketch, "E997", {"start": v(-4.82, -5.22) * mm, "end": v(-5.25, -4.8) * mm});
            skLineSegment(sketch, "E998", {"start": v(-5.25, -4.8) * mm, "end": v(-5.65, -4.45) * mm});
            skLineSegment(sketch, "E999", {"start": v(-5.65, -4.45) * mm, "end": v(-5.99, -4.18) * mm});
            skLineSegment(sketch, "E1000", {"start": v(-5.99, -4.18) * mm, "end": v(-6.26, -4.02) * mm});
            skLineSegment(sketch, "E1001", {"start": v(-6.26, -4.02) * mm, "end": v(-6.46, -4) * mm});
            skLineSegment(sketch, "E1002", {"start": v(-6.46, -4) * mm, "end": v(-6.54, -4.07) * mm});
            skLineSegment(sketch, "E1003", {"start": v(-6.54, -4.07) * mm, "end": v(-6.54, -4.1) * mm});
            skLineSegment(sketch, "E1004", {"start": v(-7.25, -0.08) * mm, "end": v(-7.26, -0.23) * mm});
            skLineSegment(sketch, "E1005", {"start": v(-7.26, -0.23) * mm, "end": v(-7.21, -0.7) * mm});
            skLineSegment(sketch, "E1006", {"start": v(-7.21, -0.7) * mm, "end": v(-7.07, -1.3) * mm});
            skLineSegment(sketch, "E1007", {"start": v(-7.07, -1.3) * mm, "end": v(-6.84, -1.85) * mm});
            skLineSegment(sketch, "E1008", {"start": v(-6.84, -1.85) * mm, "end": v(-6.56, -2.35) * mm});
            skLineSegment(sketch, "E1009", {"start": v(-6.56, -2.35) * mm, "end": v(-6.23, -2.76) * mm});
            skLineSegment(sketch, "E1010", {"start": v(-6.23, -2.76) * mm, "end": v(-5.9, -3.08) * mm});
            skLineSegment(sketch, "E1011", {"start": v(-5.9, -3.08) * mm, "end": v(-5.57, -3.29) * mm});
            skLineSegment(sketch, "E1012", {"start": v(-5.57, -3.29) * mm, "end": v(-5.34, -3.36) * mm});
            skLineSegment(sketch, "E1013", {"start": v(-5.34, -3.36) * mm, "end": v(-5.27, -3.36) * mm});
            skLineSegment(sketch, "E1014", {"start": v(-5.27, -3.36) * mm, "end": v(-5.18, -3.36) * mm});
            skLineSegment(sketch, "E1015", {"start": v(-5.18, -3.36) * mm, "end": v(-4.93, -3.3) * mm});
            skLineSegment(sketch, "E1016", {"start": v(-4.93, -3.3) * mm, "end": v(-4.6, -3.13) * mm});
            skLineSegment(sketch, "E1017", {"start": v(-4.6, -3.13) * mm, "end": v(-4.29, -2.84) * mm});
            skLineSegment(sketch, "E1018", {"start": v(-4.29, -2.84) * mm, "end": v(-4, -2.46) * mm});
            skLineSegment(sketch, "E1019", {"start": v(-4, -2.46) * mm, "end": v(-3.77, -1.98) * mm});
            skLineSegment(sketch, "E1020", {"start": v(-3.77, -1.98) * mm, "end": v(-3.58, -1.42) * mm});
            skLineSegment(sketch, "E1021", {"start": v(-3.58, -1.42) * mm, "end": v(-3.46, -0.78) * mm});
            skLineSegment(sketch, "E1022", {"start": v(-3.46, -0.78) * mm, "end": v(-3.41, -0.25) * mm});
            skLineSegment(sketch, "E1023", {"start": v(-3.41, -0.25) * mm, "end": v(-3.4, -0.07) * mm});
            skLineSegment(sketch, "E1024", {"start": v(-3.4, -0.07) * mm, "end": v(-3.4, 0.11) * mm});
            skLineSegment(sketch, "E1025", {"start": v(-3.4, 0.11) * mm, "end": v(-3.44, 0.65) * mm});
            skLineSegment(sketch, "E1026", {"start": v(-3.44, 0.65) * mm, "end": v(-3.53, 1.3) * mm});
            skLineSegment(sketch, "E1027", {"start": v(-3.53, 1.3) * mm, "end": v(-3.69, 1.86) * mm});
            skLineSegment(sketch, "E1028", {"start": v(-3.69, 1.86) * mm, "end": v(-3.9, 2.34) * mm});
            skLineSegment(sketch, "E1029", {"start": v(-3.9, 2.34) * mm, "end": v(-4.14, 2.72) * mm});
            skLineSegment(sketch, "E1030", {"start": v(-4.14, 2.72) * mm, "end": v(-4.43, 3) * mm});
            skLineSegment(sketch, "E1031", {"start": v(-4.43, 3) * mm, "end": v(-4.75, 3.17) * mm});
            skLineSegment(sketch, "E1032", {"start": v(-4.75, 3.17) * mm, "end": v(-5, 3.23) * mm});
            skLineSegment(sketch, "E1033", {"start": v(-5, 3.23) * mm, "end": v(-5.09, 3.24) * mm});
            skLineSegment(sketch, "E1034", {"start": v(-5.09, 3.24) * mm, "end": v(-5.19, 3.24) * mm});
            skLineSegment(sketch, "E1035", {"start": v(-5.19, 3.24) * mm, "end": v(-5.48, 3.16) * mm});
            skLineSegment(sketch, "E1036", {"start": v(-5.48, 3.16) * mm, "end": v(-5.87, 2.93) * mm});
            skLineSegment(sketch, "E1037", {"start": v(-5.87, 2.93) * mm, "end": v(-6.24, 2.58) * mm});
            skLineSegment(sketch, "E1038", {"start": v(-6.24, 2.58) * mm, "end": v(-6.57, 2.14) * mm});
            skLineSegment(sketch, "E1039", {"start": v(-6.57, 2.14) * mm, "end": v(-6.85, 1.62) * mm});
            skLineSegment(sketch, "E1040", {"start": v(-6.85, 1.62) * mm, "end": v(-7.07, 1.07) * mm});
            skLineSegment(sketch, "E1041", {"start": v(-7.07, 1.07) * mm, "end": v(-7.2, 0.49) * mm});
            skLineSegment(sketch, "E1042", {"start": v(-7.2, 0.49) * mm, "end": v(-7.25, 0.06) * mm});
            skLineSegment(sketch, "E1043", {"start": v(-7.25, 0.06) * mm, "end": v(-7.25, -0.08) * mm});
            skLineSegment(sketch, "E1044", {"start": v(11.32, 0.02) * mm, "end": v(11.31, 0.16) * mm});
            skLineSegment(sketch, "E1045", {"start": v(11.31, 0.16) * mm, "end": v(11.32, 0.59) * mm});
            skLineSegment(sketch, "E1046", {"start": v(11.32, 0.59) * mm, "end": v(11.38, 1.17) * mm});
            skLineSegment(sketch, "E1047", {"start": v(11.38, 1.17) * mm, "end": v(11.48, 1.74) * mm});
            skLineSegment(sketch, "E1048", {"start": v(11.48, 1.74) * mm, "end": v(11.62, 2.28) * mm});
            skLineSegment(sketch, "E1049", {"start": v(11.62, 2.28) * mm, "end": v(11.8, 2.74) * mm});
            skLineSegment(sketch, "E1050", {"start": v(11.8, 2.74) * mm, "end": v(12, 3.11) * mm});
            skLineSegment(sketch, "E1051", {"start": v(12, 3.11) * mm, "end": v(12.24, 3.35) * mm});
            skLineSegment(sketch, "E1052", {"start": v(12.24, 3.35) * mm, "end": v(12.43, 3.44) * mm});
            skLineSegment(sketch, "E1053", {"start": v(12.43, 3.44) * mm, "end": v(12.5, 3.44) * mm});
            skLineSegment(sketch, "E1054", {"start": v(12.5, 3.44) * mm, "end": v(12.57, 3.44) * mm});
            skLineSegment(sketch, "E1055", {"start": v(12.57, 3.44) * mm, "end": v(12.8, 3.37) * mm});
            skLineSegment(sketch, "E1056", {"start": v(12.8, 3.37) * mm, "end": v(13.14, 3.15) * mm});
            skLineSegment(sketch, "E1057", {"start": v(13.14, 3.15) * mm, "end": v(13.5, 2.8) * mm});
            skLineSegment(sketch, "E1058", {"start": v(13.5, 2.8) * mm, "end": v(13.87, 2.35) * mm});
            skLineSegment(sketch, "E1059", {"start": v(13.87, 2.35) * mm, "end": v(14.2, 1.8) * mm});
            skLineSegment(sketch, "E1060", {"start": v(14.2, 1.8) * mm, "end": v(14.47, 1.21) * mm});
            skLineSegment(sketch, "E1061", {"start": v(14.47, 1.21) * mm, "end": v(14.65, 0.58) * mm});
            skLineSegment(sketch, "E1062", {"start": v(14.65, 0.58) * mm, "end": v(14.7, 0.09) * mm});
            skLineSegment(sketch, "E1063", {"start": v(14.7, 0.09) * mm, "end": v(14.7, -0.07) * mm});
            skLineSegment(sketch, "E1064", {"start": v(14.7, -0.07) * mm, "end": v(14.71, -0.24) * mm});
            skLineSegment(sketch, "E1065", {"start": v(14.71, -0.24) * mm, "end": v(14.66, -0.75) * mm});
            skLineSegment(sketch, "E1066", {"start": v(14.66, -0.75) * mm, "end": v(14.5, -1.4) * mm});
            skLineSegment(sketch, "E1067", {"start": v(14.5, -1.4) * mm, "end": v(14.25, -2) * mm});
            skLineSegment(sketch, "E1068", {"start": v(14.25, -2) * mm, "end": v(13.93, -2.53) * mm});
            skLineSegment(sketch, "E1069", {"start": v(13.93, -2.53) * mm, "end": v(13.59, -2.99) * mm});
            skLineSegment(sketch, "E1070", {"start": v(13.59, -2.99) * mm, "end": v(13.24, -3.33) * mm});
            skLineSegment(sketch, "E1071", {"start": v(13.24, -3.33) * mm, "end": v(12.94, -3.55) * mm});
            skLineSegment(sketch, "E1072", {"start": v(12.94, -3.55) * mm, "end": v(12.75, -3.63) * mm});
            skLineSegment(sketch, "E1073", {"start": v(12.75, -3.63) * mm, "end": v(12.7, -3.62) * mm});
            skLineSegment(sketch, "E1074", {"start": v(12.7, -3.62) * mm, "end": v(12.62, -3.63) * mm});
            skLineSegment(sketch, "E1075", {"start": v(12.62, -3.63) * mm, "end": v(12.4, -3.53) * mm});
            skLineSegment(sketch, "E1076", {"start": v(12.4, -3.53) * mm, "end": v(12.14, -3.27) * mm});
            skLineSegment(sketch, "E1077", {"start": v(12.14, -3.27) * mm, "end": v(11.9, -2.86) * mm});
            skLineSegment(sketch, "E1078", {"start": v(11.9, -2.86) * mm, "end": v(11.7, -2.35) * mm});
            skLineSegment(sketch, "E1079", {"start": v(11.7, -2.35) * mm, "end": v(11.53, -1.77) * mm});
            skLineSegment(sketch, "E1080", {"start": v(11.53, -1.77) * mm, "end": v(11.4, -1.16) * mm});
            skLineSegment(sketch, "E1081", {"start": v(11.4, -1.16) * mm, "end": v(11.34, -0.55) * mm});
            skLineSegment(sketch, "E1082", {"start": v(11.34, -0.55) * mm, "end": v(11.32, -0.12) * mm});
            skLineSegment(sketch, "E1083", {"start": v(11.32, -0.12) * mm, "end": v(11.32, 0.02) * mm});
            skLineSegment(sketch, "E1084", {"start": v(7.13, -5.36) * mm, "end": v(7.25, -5.27) * mm});
            skLineSegment(sketch, "E1085", {"start": v(7.25, -5.27) * mm, "end": v(7.63, -5) * mm});
            skLineSegment(sketch, "E1086", {"start": v(7.63, -5) * mm, "end": v(8.2, -4.7) * mm});
            skLineSegment(sketch, "E1087", {"start": v(8.2, -4.7) * mm, "end": v(8.8, -4.48) * mm});
            skLineSegment(sketch, "E1088", {"start": v(8.8, -4.48) * mm, "end": v(9.4, -4.33) * mm});
            skLineSegment(sketch, "E1089", {"start": v(9.4, -4.33) * mm, "end": v(9.97, -4.27) * mm});
            skLineSegment(sketch, "E1090", {"start": v(9.97, -4.27) * mm, "end": v(10.49, -4.3) * mm});
            skLineSegment(sketch, "E1091", {"start": v(10.49, -4.3) * mm, "end": v(10.91, -4.46) * mm});
            skLineSegment(sketch, "E1092", {"start": v(10.91, -4.46) * mm, "end": v(11.16, -4.64) * mm});
            skLineSegment(sketch, "E1093", {"start": v(11.16, -4.64) * mm, "end": v(11.22, -4.72) * mm});
            skLineSegment(sketch, "E1094", {"start": v(11.22, -4.72) * mm, "end": v(11.27, -4.8) * mm});
            skLineSegment(sketch, "E1095", {"start": v(11.27, -4.8) * mm, "end": v(11.37, -5.08) * mm});
            skLineSegment(sketch, "E1096", {"start": v(11.37, -5.08) * mm, "end": v(11.45, -5.53) * mm});
            skLineSegment(sketch, "E1097", {"start": v(11.45, -5.53) * mm, "end": v(11.42, -6.04) * mm});
            skLineSegment(sketch, "E1098", {"start": v(11.42, -6.04) * mm, "end": v(11.3, -6.6) * mm});
            skLineSegment(sketch, "E1099", {"start": v(11.3, -6.6) * mm, "end": v(11.06, -7.2) * mm});
            skLineSegment(sketch, "E1100", {"start": v(11.06, -7.2) * mm, "end": v(10.68, -7.8) * mm});
            skLineSegment(sketch, "E1101", {"start": v(10.68, -7.8) * mm, "end": v(10.16, -8.4) * mm});
            skLineSegment(sketch, "E1102", {"start": v(10.16, -8.4) * mm, "end": v(9.66, -8.82) * mm});
            skLineSegment(sketch, "E1103", {"start": v(9.66, -8.82) * mm, "end": v(9.48, -8.95) * mm});
            skLineSegment(sketch, "E1104", {"start": v(9.48, -8.95) * mm, "end": v(9.33, -9.03) * mm});
            skLineSegment(sketch, "E1105", {"start": v(9.33, -9.03) * mm, "end": v(8.84, -9.25) * mm});
            skLineSegment(sketch, "E1106", {"start": v(8.84, -9.25) * mm, "end": v(8.22, -9.47) * mm});
            skLineSegment(sketch, "E1107", {"start": v(8.22, -9.47) * mm, "end": v(7.62, -9.6) * mm});
            skLineSegment(sketch, "E1108", {"start": v(7.62, -9.6) * mm, "end": v(7.06, -9.64) * mm});
            skLineSegment(sketch, "E1109", {"start": v(7.06, -9.64) * mm, "end": v(6.55, -9.6) * mm});
            skLineSegment(sketch, "E1110", {"start": v(6.55, -9.6) * mm, "end": v(6.12, -9.5) * mm});
            skLineSegment(sketch, "E1111", {"start": v(6.12, -9.5) * mm, "end": v(5.78, -9.33) * mm});
            skLineSegment(sketch, "E1112", {"start": v(5.78, -9.33) * mm, "end": v(5.58, -9.17) * mm});
            skLineSegment(sketch, "E1113", {"start": v(5.58, -9.17) * mm, "end": v(5.53, -9.1) * mm});
            skLineSegment(sketch, "E1114", {"start": v(5.53, -9.1) * mm, "end": v(5.47, -9.02) * mm});
            skLineSegment(sketch, "E1115", {"start": v(5.47, -9.02) * mm, "end": v(5.37, -8.7) * mm});
            skLineSegment(sketch, "E1116", {"start": v(5.37, -8.7) * mm, "end": v(5.33, -8.27) * mm});
            skLineSegment(sketch, "E1117", {"start": v(5.33, -8.27) * mm, "end": v(5.4, -7.8) * mm});
            skLineSegment(sketch, "E1118", {"start": v(5.4, -7.8) * mm, "end": v(5.58, -7.3) * mm});
            skLineSegment(sketch, "E1119", {"start": v(5.58, -7.3) * mm, "end": v(5.85, -6.8) * mm});
            skLineSegment(sketch, "E1120", {"start": v(5.85, -6.8) * mm, "end": v(6.2, -6.31) * mm});
            skLineSegment(sketch, "E1121", {"start": v(6.2, -6.31) * mm, "end": v(6.64, -5.83) * mm});
            skLineSegment(sketch, "E1122", {"start": v(6.64, -5.83) * mm, "end": v(7, -5.47) * mm});
            skLineSegment(sketch, "E1123", {"start": v(7, -5.47) * mm, "end": v(7.13, -5.36) * mm});
            skLineSegment(sketch, "E1124", {"start": v(6.73, 5.2) * mm, "end": v(6.86, 5.1) * mm});
            skLineSegment(sketch, "E1125", {"start": v(6.86, 5.1) * mm, "end": v(7.27, 4.8) * mm});
            skLineSegment(sketch, "E1126", {"start": v(7.27, 4.8) * mm, "end": v(7.88, 4.47) * mm});
            skLineSegment(sketch, "E1127", {"start": v(7.88, 4.47) * mm, "end": v(8.52, 4.2) * mm});
            skLineSegment(sketch, "E1128", {"start": v(8.52, 4.2) * mm, "end": v(9.18, 4) * mm});
            skLineSegment(sketch, "E1129", {"start": v(9.18, 4) * mm, "end": v(9.8, 3.9) * mm});
            skLineSegment(sketch, "E1130", {"start": v(9.8, 3.9) * mm, "end": v(10.38, 3.91) * mm});
            skLineSegment(sketch, "E1131", {"start": v(10.38, 3.91) * mm, "end": v(10.86, 4.03) * mm});
            skLineSegment(sketch, "E1132", {"start": v(10.86, 4.03) * mm, "end": v(11.15, 4.2) * mm});
            skLineSegment(sketch, "E1133", {"start": v(11.15, 4.2) * mm, "end": v(11.22, 4.27) * mm});
            skLineSegment(sketch, "E1134", {"start": v(11.22, 4.27) * mm, "end": v(11.28, 4.35) * mm});
            skLineSegment(sketch, "E1135", {"start": v(11.28, 4.35) * mm, "end": v(11.4, 4.62) * mm});
            skLineSegment(sketch, "E1136", {"start": v(11.4, 4.62) * mm, "end": v(11.52, 5.08) * mm});
            skLineSegment(sketch, "E1137", {"start": v(11.52, 5.08) * mm, "end": v(11.53, 5.61) * mm});
            skLineSegment(sketch, "E1138", {"start": v(11.53, 5.61) * mm, "end": v(11.43, 6.2) * mm});
            skLineSegment(sketch, "E1139", {"start": v(11.43, 6.2) * mm, "end": v(11.2, 6.83) * mm});
            skLineSegment(sketch, "E1140", {"start": v(11.2, 6.83) * mm, "end": v(10.83, 7.47) * mm});
            skLineSegment(sketch, "E1141", {"start": v(10.83, 7.47) * mm, "end": v(10.3, 8.1) * mm});
            skLineSegment(sketch, "E1142", {"start": v(10.3, 8.1) * mm, "end": v(9.77, 8.58) * mm});
            skLineSegment(sketch, "E1143", {"start": v(9.77, 8.58) * mm, "end": v(9.58, 8.71) * mm});
            skLineSegment(sketch, "E1144", {"start": v(9.58, 8.71) * mm, "end": v(9.45, 8.82) * mm});
            skLineSegment(sketch, "E1145", {"start": v(9.45, 8.82) * mm, "end": v(9, 9.07) * mm});
            skLineSegment(sketch, "E1146", {"start": v(9, 9.07) * mm, "end": v(8.35, 9.3) * mm});
            skLineSegment(sketch, "E1147", {"start": v(8.35, 9.3) * mm, "end": v(7.69, 9.41) * mm});
            skLineSegment(sketch, "E1148", {"start": v(7.69, 9.41) * mm, "end": v(7.02, 9.43) * mm});
            skLineSegment(sketch, "E1149", {"start": v(7.02, 9.43) * mm, "end": v(6.4, 9.37) * mm});
            skLineSegment(sketch, "E1150", {"start": v(6.4, 9.37) * mm, "end": v(5.84, 9.23) * mm});
            skLineSegment(sketch, "E1151", {"start": v(5.84, 9.23) * mm, "end": v(5.39, 9.05) * mm});
            skLineSegment(sketch, "E1152", {"start": v(5.39, 9.05) * mm, "end": v(5.14, 8.89) * mm});
            skLineSegment(sketch, "E1153", {"start": v(5.14, 8.89) * mm, "end": v(5.07, 8.82) * mm});
            skLineSegment(sketch, "E1154", {"start": v(5.07, 8.82) * mm, "end": v(5, 8.74) * mm});
            skLineSegment(sketch, "E1155", {"start": v(5, 8.74) * mm, "end": v(4.87, 8.44) * mm});
            skLineSegment(sketch, "E1156", {"start": v(4.87, 8.44) * mm, "end": v(4.81, 8.03) * mm});
            skLineSegment(sketch, "E1157", {"start": v(4.81, 8.03) * mm, "end": v(4.89, 7.6) * mm});
            skLineSegment(sketch, "E1158", {"start": v(4.89, 7.6) * mm, "end": v(5.08, 7.13) * mm});
            skLineSegment(sketch, "E1159", {"start": v(5.08, 7.13) * mm, "end": v(5.37, 6.66) * mm});
            skLineSegment(sketch, "E1160", {"start": v(5.37, 6.66) * mm, "end": v(5.75, 6.17) * mm});
            skLineSegment(sketch, "E1161", {"start": v(5.75, 6.17) * mm, "end": v(6.21, 5.69) * mm});
            skLineSegment(sketch, "E1162", {"start": v(6.21, 5.69) * mm, "end": v(6.6, 5.32) * mm});
            skLineSegment(sketch, "E1163", {"start": v(6.6, 5.32) * mm, "end": v(6.73, 5.2) * mm});
            skLineSegment(sketch, "E1164", {"start": v(6.73, 5.2) * mm, "end": v(6.73, 5.2) * mm});
            skSolve(sketch);
        }
        {
            var Q0;
            Q0 = qSketchRegion(id + "F12", true);
            var Q1;
            Q1=makeQuery(id+"F12.imprint","IMPRINT",FACE,{"disambiguationData":[TD([[makeQuery(id+"F12.imprint","IMPRINT",EDGE,{"derivedFrom":sQuery(id+"F12.wireOp",EDGE,"E28")}),-1.0]])]});
            var Q2;
            Q2=makeQuery(id+"F12.imprint","IMPRINT",FACE,{"disambiguationData":[TD([[makeQuery(id+"F12.imprint","IMPRINT",EDGE,{"derivedFrom":sQuery(id+"F12.wireOp",EDGE,"E28")}),1.0]])]});
            var Q3;
            Q3=makeQuery(id+"F12.imprint","IMPRINT",FACE,{"disambiguationData":[TD([[makeQuery(id+"F12.imprint","IMPRINT",EDGE,{"derivedFrom":sQuery(id+"F12.wireOp",EDGE,"E31")}),1.0]])]});
            var Q4;
            Q4=makeQuery(id+"F12.imprint","IMPRINT",FACE,{"disambiguationData":[TD([[makeQuery(id+"F12.imprint","IMPRINT",EDGE,{"derivedFrom":sQuery(id+"F12.wireOp",EDGE,"E31")}),-1.0]])]});
            var Q5;
            Q5=makeQuery(id+"F12.imprint","IMPRINT",FACE,{"disambiguationData":[TD([[makeQuery(id+"F12.imprint","IMPRINT",EDGE,{"derivedFrom":sQuery(id+"F12.wireOp",EDGE,"E30")}),-1.0]])]});
            var Q6;
            Q6=makeQuery(id+"F12.imprint","IMPRINT",FACE,{"disambiguationData":[TD([[makeQuery(id+"F12.imprint","IMPRINT",EDGE,{"derivedFrom":sQuery(id+"F12.wireOp",EDGE,"E30")}),1.0]])]});
            var Q7;
            Q7=makeQuery(id+"F12.imprint","IMPRINT",FACE,{"disambiguationData":[TD([[makeQuery(id+"F12.imprint","IMPRINT",EDGE,{"derivedFrom":sQuery(id+"F12.wireOp",EDGE,"E29")}),-1.0]])]});
            var Q8;
            Q8=makeQuery(id+"F12.imprint","IMPRINT",FACE,{"disambiguationData":[TD([[makeQuery(id+"F12.imprint","IMPRINT",EDGE,{"derivedFrom":sQuery(id+"F12.wireOp",EDGE,"E29")}),1.0]])]});
            extrude(context, id + "F23", {"entities" : qUnion([Q0, Q1, Q2, Q3, Q4, Q5, Q6, Q7, Q8]), "depth" : 7 * mm, "offsetDistance" : 25 * mm, "hasSecondDirection" : true, "secondDirectionOppositeDirection" : false, "secondDirectionDepth" : 6.1 * mm});
        }
        {
            var Q0;
            Q0=makeQuery(id+"F12.imprint","IMPRINT",FACE,{"disambiguationData":[TD([[makeQuery(id+"F12.imprint","IMPRINT",EDGE,{"derivedFrom":sQuery(id+"F12.wireOp",EDGE,"E28")}),-1.0]])]});
            var Q1;
            Q1=makeQuery(id+"F12.imprint","IMPRINT",FACE,{"disambiguationData":[TD([[makeQuery(id+"F12.imprint","IMPRINT",EDGE,{"derivedFrom":sQuery(id+"F12.wireOp",EDGE,"E31")}),-1.0]])]});
            var Q2;
            Q2=makeQuery(id+"F12.imprint","IMPRINT",FACE,{"disambiguationData":[TD([[makeQuery(id+"F12.imprint","IMPRINT",EDGE,{"derivedFrom":sQuery(id+"F12.wireOp",EDGE,"E30")}),-1.0]])]});
            var Q3;
            Q3=makeQuery(id+"F12.imprint","IMPRINT",FACE,{"disambiguationData":[TD([[makeQuery(id+"F12.imprint","IMPRINT",EDGE,{"derivedFrom":sQuery(id+"F12.wireOp",EDGE,"E29")}),-1.0]])]});
            var Q4;
            Q4=sQuery(id+"F12.wireOp",EDGE,"E32");
            var Q5;
            Q5=sQuery(id+"F12.wireOp",EDGE,"E28");
            extrude(context, id + "F24", {"entities" : qUnion([Q0, Q1, Q2, Q3]), "operationType" : NewBodyOperationType.ADD, "surfaceEntities" : qUnion([Q4, Q5]), "depth" : 6.1 * mm, "offsetDistance" : 25 * mm, "hasSecondDirection" : true, "secondDirectionOppositeDirection" : false, "secondDirectionDepth" : 3 * mm});
        }
        {
            var Q0;
            Q0 = qSketchRegion(id + "F22", true);
            extrude(context, id + "F25", {"entities" : qUnion([Q0]), "operationType" : NewBodyOperationType.REMOVE, "depth" : 7.1 * mm, "offsetDistance" : 25 * mm, "hasSecondDirection" : true, "secondDirectionOppositeDirection" : false, "secondDirectionDepth" : 6.8 * mm});
        }
    });
